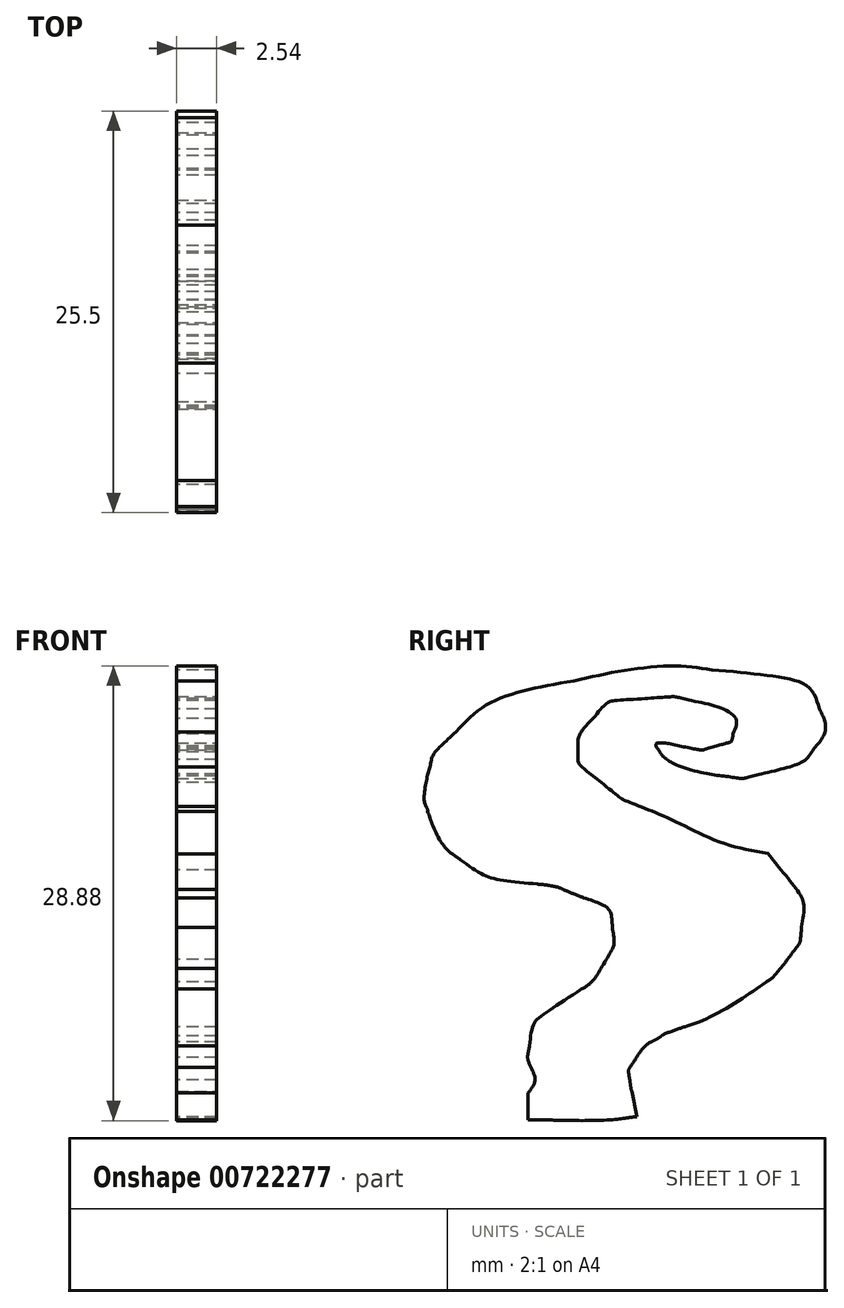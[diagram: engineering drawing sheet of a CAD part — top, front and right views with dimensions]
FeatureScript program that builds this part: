
annotation { "Feature Type Name" : "Feature", "Feature Type Description" : "" }
export const myFeature = defineFeature(function(context is Context, id is Id, definition is map)
    precondition{}
    {
        {
            var Q0;
            Q0=qCreatedBy(makeId("Right.planeOp"),FACE);
            var sketch = newSketch(context, id + "F0", { "sketchPlane" : qUnion([Q0])});
            skFitSpline(sketch, "E0", {"points": [v(-62.42, -40.65) * mm, v(-62.37, -40.57) * mm, v(-62.3, -40.5) * mm, v(-62.27, -40.5) * mm]});
            skFitSpline(sketch, "E1", {"points": [v(-62.27, -40.5) * mm, v(-62.23, -40.5) * mm, v(-62.2, -40.57) * mm, v(-62.2, -40.65) * mm]});
            skFitSpline(sketch, "E2", {"points": [v(-62.2, -40.65) * mm, v(-62.2, -40.73) * mm, v(-62.27, -40.8) * mm, v(-62.35, -40.8) * mm]});
            skFitSpline(sketch, "E3", {"points": [v(-62.35, -40.8) * mm, v(-62.44, -40.8) * mm, v(-62.46, -40.73) * mm, v(-62.42, -40.65) * mm]});
            skFitSpline(sketch, "E4", {"points": [v(6.95, -37.34) * mm, v(6.67, -37.22) * mm, v(6.74, -36.81) * mm, v(7.12, -36.25) * mm]});
            skFitSpline(sketch, "E5", {"points": [v(7.12, -36.25) * mm, v(7.31, -35.96) * mm, v(7.47, -35.66) * mm, v(7.47, -35.58) * mm]});
            skFitSpline(sketch, "E6", {"points": [v(7.47, -35.58) * mm, v(7.47, -35.5) * mm, v(7.56, -35.27) * mm, v(7.68, -35.06) * mm]});
            skFitSpline(sketch, "E7", {"points": [v(7.68, -35.06) * mm, v(7.79, -34.86) * mm, v(8.01, -34.38) * mm, v(8.17, -34) * mm]});
            skFitSpline(sketch, "E8", {"points": [v(8.17, -34) * mm, v(8.34, -33.6) * mm, v(8.53, -33.16) * mm, v(8.6, -33) * mm]});
            skFitSpline(sketch, "E9", {"points": [v(8.6, -33) * mm, v(8.67, -32.85) * mm, v(8.9, -32.16) * mm, v(9.13, -31.46) * mm]});
            skFitSpline(sketch, "E10", {"points": [v(9.13, -31.46) * mm, v(9.36, -30.76) * mm, v(9.6, -30.07) * mm, v(9.68, -29.92) * mm]});
            skFitSpline(sketch, "E11", {"points": [v(9.68, -29.92) * mm, v(9.76, -29.77) * mm, v(9.9, -29.36) * mm, v(9.99, -29.01) * mm]});
            skFitSpline(sketch, "E12", {"points": [v(9.99, -29.01) * mm, v(10.24, -28.04) * mm, v(10.5, -27.21) * mm, v(10.9, -26.14) * mm]});
            skFitSpline(sketch, "E13", {"points": [v(10.9, -26.14) * mm, v(11.1, -25.6) * mm, v(11.25, -25.03) * mm, v(11.25, -24.88) * mm]});
            skFitSpline(sketch, "E14", {"points": [v(11.25, -24.88) * mm, v(11.26, -24.72) * mm, v(11.38, -24.4) * mm, v(11.54, -24.18) * mm]});
            skFitSpline(sketch, "E15", {"points": [v(11.54, -24.18) * mm, v(11.7, -23.95) * mm, v(11.82, -23.56) * mm, v(11.82, -23.33) * mm]});
            skFitSpline(sketch, "E16", {"points": [v(11.82, -23.33) * mm, v(11.82, -23.1) * mm, v(11.91, -22.78) * mm, v(12.02, -22.63) * mm]});
            skFitSpline(sketch, "E17", {"points": [v(12.02, -22.63) * mm, v(12.14, -22.48) * mm, v(12.23, -22.2) * mm, v(12.23, -22) * mm]});
            skFitSpline(sketch, "E18", {"points": [v(12.23, -22) * mm, v(12.24, -21.8) * mm, v(12.33, -21.51) * mm, v(12.44, -21.36) * mm]});
            skFitSpline(sketch, "E19", {"points": [v(12.44, -21.36) * mm, v(12.56, -21.22) * mm, v(12.65, -20.87) * mm, v(12.65, -20.6) * mm]});
            skFitSpline(sketch, "E20", {"points": [v(12.65, -20.6) * mm, v(12.66, -20.33) * mm, v(12.74, -19.98) * mm, v(12.85, -19.83) * mm]});
            skFitSpline(sketch, "E21", {"points": [v(12.85, -19.83) * mm, v(12.95, -19.67) * mm, v(13.08, -19.3) * mm, v(13.12, -19) * mm]});
            skFitSpline(sketch, "E22", {"points": [v(13.12, -19) * mm, v(13.17, -18.7) * mm, v(13.33, -18.14) * mm, v(13.48, -17.74) * mm]});
            skFitSpline(sketch, "E23", {"points": [v(13.48, -17.74) * mm, v(13.92, -16.59) * mm, v(14.06, -16.05) * mm, v(14.06, -15.6) * mm]});
            skFitSpline(sketch, "E24", {"points": [v(14.06, -15.6) * mm, v(14.06, -15.36) * mm, v(14.19, -15.01) * mm, v(14.34, -14.81) * mm]});
            skFitSpline(sketch, "E25", {"points": [v(14.34, -14.81) * mm, v(14.51, -14.6) * mm, v(14.61, -14.28) * mm, v(14.6, -14.03) * mm]});
            skFitSpline(sketch, "E26", {"points": [v(14.6, -14.03) * mm, v(14.58, -13.78) * mm, v(14.67, -13.5) * mm, v(14.83, -13.32) * mm]});
            skFitSpline(sketch, "E27", {"points": [v(14.83, -13.32) * mm, v(14.98, -13.14) * mm, v(15.04, -12.98) * mm, v(14.96, -12.9) * mm]});
            skFitSpline(sketch, "E28", {"points": [v(14.96, -12.9) * mm, v(14.9, -12.85) * mm, v(14.01, -12.72) * mm, v(13, -12.63) * mm]});
            skFitSpline(sketch, "E29", {"points": [v(13, -12.63) * mm, v(10.97, -12.45) * mm, v(10.77, -12.35) * mm, v(10.99, -11.58) * mm]});
            skFitSpline(sketch, "E30", {"points": [v(10.99, -11.58) * mm, v(11.06, -11.34) * mm, v(11.23, -10.98) * mm, v(11.38, -10.79) * mm]});
            skFitSpline(sketch, "E31", {"points": [v(11.38, -10.79) * mm, v(11.63, -10.45) * mm, v(11.7, -10.44) * mm, v(13.33, -10.41) * mm]});
            skFitSpline(sketch, "E32", {"points": [v(13.33, -10.41) * mm, v(15.37, -10.38) * mm, v(15.88, -10.2) * mm, v(15.88, -9.49) * mm]});
            skFitSpline(sketch, "E33", {"points": [v(15.88, -9.49) * mm, v(15.88, -9.24) * mm, v(16.01, -8.85) * mm, v(16.16, -8.62) * mm]});
            skFitSpline(sketch, "E34", {"points": [v(16.16, -8.62) * mm, v(16.32, -8.38) * mm, v(16.44, -8.06) * mm, v(16.44, -7.9) * mm]});
            skFitSpline(sketch, "E35", {"points": [v(16.44, -7.9) * mm, v(16.44, -7.73) * mm, v(16.53, -7.52) * mm, v(16.65, -7.43) * mm]});
            skFitSpline(sketch, "E36", {"points": [v(16.65, -7.43) * mm, v(16.76, -7.34) * mm, v(16.89, -7.08) * mm, v(16.93, -6.86) * mm]});
            skFitSpline(sketch, "E37", {"points": [v(16.93, -6.86) * mm, v(16.98, -6.64) * mm, v(17.11, -6.39) * mm, v(17.22, -6.3) * mm]});
            skFitSpline(sketch, "E38", {"points": [v(17.22, -6.3) * mm, v(17.33, -6.2) * mm, v(17.43, -6.07) * mm, v(17.43, -6) * mm]});
            skFitSpline(sketch, "E39", {"points": [v(17.43, -6) * mm, v(17.43, -5.66) * mm, v(19.5, -3.04) * mm, v(20.14, -2.56) * mm]});
            skFitSpline(sketch, "E40", {"points": [v(20.14, -2.56) * mm, v(21.45, -1.6) * mm, v(22.48, -0.98) * mm, v(23.02, -0.84) * mm]});
            skFitSpline(sketch, "E41", {"points": [v(23.02, -0.84) * mm, v(23.36, -0.75) * mm, v(23.77, -0.59) * mm, v(23.93, -0.49) * mm]});
            skFitSpline(sketch, "E42", {"points": [v(23.93, -0.49) * mm, v(24.1, -0.38) * mm, v(24.92, -0.26) * mm, v(25.86, -0.2) * mm]});
            skFitSpline(sketch, "E43", {"points": [v(25.86, -0.2) * mm, v(27.2, -0.13) * mm, v(27.57, -0.15) * mm, v(27.92, -0.33) * mm]});
            skFitSpline(sketch, "E44", {"points": [v(27.92, -0.33) * mm, v(28.16, -0.46) * mm, v(28.58, -0.55) * mm, v(28.86, -0.55) * mm]});
            skFitSpline(sketch, "E45", {"points": [v(28.86, -0.55) * mm, v(29.16, -0.55) * mm, v(29.52, -0.67) * mm, v(29.72, -0.83) * mm]});
            skFitSpline(sketch, "E46", {"points": [v(29.72, -0.83) * mm, v(29.92, -0.99) * mm, v(30.16, -1.11) * mm, v(30.27, -1.11) * mm]});
            skFitSpline(sketch, "E47", {"points": [v(30.27, -1.11) * mm, v(30.5, -1.11) * mm, v(31.44, -1.93) * mm, v(31.44, -2.14) * mm]});
            skFitSpline(sketch, "E48", {"points": [v(31.44, -2.14) * mm, v(31.44, -2.22) * mm, v(31.56, -2.42) * mm, v(31.7, -2.58) * mm]});
            skFitSpline(sketch, "E49", {"points": [v(31.7, -2.58) * mm, v(31.89, -2.78) * mm, v(32, -3.16) * mm, v(32.04, -3.81) * mm]});
            skFitSpline(sketch, "E50", {"points": [v(32.04, -3.81) * mm, v(32.1, -4.6) * mm, v(32.07, -4.8) * mm, v(31.85, -5.06) * mm]});
            skFitSpline(sketch, "E51", {"points": [v(31.85, -5.06) * mm, v(31.7, -5.23) * mm, v(31.58, -5.46) * mm, v(31.58, -5.59) * mm]});
            skFitSpline(sketch, "E52", {"points": [v(31.58, -5.59) * mm, v(31.57, -5.94) * mm, v(30.98, -6.52) * mm, v(30.24, -6.92) * mm]});
            skFitSpline(sketch, "E53", {"points": [v(30.24, -6.92) * mm, v(29.43, -7.35) * mm, v(29.36, -7.35) * mm, v(28.2, -7.06) * mm]});
            skFitSpline(sketch, "E54", {"points": [v(28.2, -7.06) * mm, v(27.03, -6.76) * mm, v(26.89, -6.67) * mm, v(26.4, -6) * mm]});
            skFitSpline(sketch, "E55", {"points": [v(26.4, -6) * mm, v(25.84, -5.23) * mm, v(25.86, -4.7) * mm, v(26.48, -3.42) * mm]});
            skFitSpline(sketch, "E56", {"points": [v(26.48, -3.42) * mm, v(26.76, -2.85) * mm, v(26.95, -2.29) * mm, v(26.9, -2.17) * mm]});
            skFitSpline(sketch, "E57", {"points": [v(26.9, -2.17) * mm, v(26.78, -1.82) * mm, v(25.62, -1.89) * mm, v(25.1, -2.27) * mm]});
            skFitSpline(sketch, "E58", {"points": [v(25.1, -2.27) * mm, v(23.94, -3.14) * mm, v(22.61, -5.14) * mm, v(22.61, -6.04) * mm]});
            skFitSpline(sketch, "E59", {"points": [v(22.61, -6.04) * mm, v(22.61, -6.24) * mm, v(22.52, -6.49) * mm, v(22.4, -6.58) * mm]});
            skFitSpline(sketch, "E60", {"points": [v(22.4, -6.58) * mm, v(22.3, -6.67) * mm, v(22.16, -6.98) * mm, v(22.12, -7.26) * mm]});
            skFitSpline(sketch, "E61", {"points": [v(22.12, -7.26) * mm, v(22.07, -7.54) * mm, v(21.94, -8) * mm, v(21.84, -8.26) * mm]});
            skFitSpline(sketch, "E62", {"points": [v(21.84, -8.26) * mm, v(21.67, -8.68) * mm, v(21.57, -9.63) * mm, v(21.62, -10.34) * mm]});
            skFitSpline(sketch, "E63", {"points": [v(21.62, -10.34) * mm, v(21.63, -10.5) * mm, v(22.02, -10.52) * mm, v(23.65, -10.45) * mm]});
            skFitSpline(sketch, "E64", {"points": [v(23.65, -10.45) * mm, v(24.75, -10.4) * mm, v(25.76, -10.34) * mm, v(25.88, -10.29) * mm]});
            skFitSpline(sketch, "E65", {"points": [v(25.88, -10.29) * mm, v(26.45, -10.07) * mm, v(26.93, -10.83) * mm, v(26.47, -11.2) * mm]});
            skFitSpline(sketch, "E66", {"points": [v(26.47, -11.2) * mm, v(26.35, -11.3) * mm, v(26.26, -11.6) * mm, v(26.26, -11.85) * mm]});
            skFitSpline(sketch, "E67", {"points": [v(26.26, -11.85) * mm, v(26.26, -12.6) * mm, v(25.78, -12.72) * mm, v(22.8, -12.8) * mm]});
            skFitSpline(sketch, "E68", {"points": [v(22.8, -12.8) * mm, v(21.06, -12.85) * mm, v(20.79, -12.96) * mm, v(20.79, -13.62) * mm]});
            skFitSpline(sketch, "E69", {"points": [v(20.79, -13.62) * mm, v(20.79, -13.85) * mm, v(20.71, -14.17) * mm, v(20.62, -14.34) * mm]});
            skFitSpline(sketch, "E70", {"points": [v(20.62, -14.34) * mm, v(20.53, -14.5) * mm, v(20.41, -14.93) * mm, v(20.36, -15.27) * mm]});
            skFitSpline(sketch, "E71", {"points": [v(20.36, -15.27) * mm, v(20.3, -15.62) * mm, v(20.2, -16.1) * mm, v(20.12, -16.33) * mm]});
            skFitSpline(sketch, "E72", {"points": [v(20.12, -16.33) * mm, v(20.04, -16.56) * mm, v(19.9, -17.01) * mm, v(19.82, -17.34) * mm]});
            skFitSpline(sketch, "E73", {"points": [v(19.82, -17.34) * mm, v(19.74, -17.67) * mm, v(19.6, -18.2) * mm, v(19.51, -18.53) * mm]});
            skFitSpline(sketch, "E74", {"points": [v(19.51, -18.53) * mm, v(19.43, -18.86) * mm, v(19.27, -19.3) * mm, v(19.16, -19.53) * mm]});
            skFitSpline(sketch, "E75", {"points": [v(19.16, -19.53) * mm, v(19.06, -19.75) * mm, v(18.97, -20.14) * mm, v(18.97, -20.41) * mm]});
            skFitSpline(sketch, "E76", {"points": [v(18.97, -20.41) * mm, v(18.97, -20.68) * mm, v(18.9, -21.02) * mm, v(18.82, -21.17) * mm]});
            skFitSpline(sketch, "E77", {"points": [v(18.82, -21.17) * mm, v(18.74, -21.33) * mm, v(18.54, -21.94) * mm, v(18.39, -22.53) * mm]});
            skFitSpline(sketch, "E78", {"points": [v(18.39, -22.53) * mm, v(17.96, -24.13) * mm, v(17.9, -24.36) * mm, v(17.57, -25.44) * mm]});
            skFitSpline(sketch, "E79", {"points": [v(17.57, -25.44) * mm, v(17.4, -25.98) * mm, v(17.2, -26.7) * mm, v(17.14, -27.05) * mm]});
            skFitSpline(sketch, "E80", {"points": [v(17.14, -27.05) * mm, v(17.06, -27.4) * mm, v(16.91, -27.87) * mm, v(16.8, -28.1) * mm]});
            skFitSpline(sketch, "E81", {"points": [v(16.8, -28.1) * mm, v(16.7, -28.33) * mm, v(16.5, -29) * mm, v(16.37, -29.57) * mm]});
            skFitSpline(sketch, "E82", {"points": [v(16.37, -29.57) * mm, v(16.23, -30.15) * mm, v(16.03, -30.75) * mm, v(15.93, -30.9) * mm]});
            skFitSpline(sketch, "E83", {"points": [v(15.93, -30.9) * mm, v(15.83, -31.05) * mm, v(15.74, -31.37) * mm, v(15.74, -31.6) * mm]});
            skFitSpline(sketch, "E84", {"points": [v(15.74, -31.6) * mm, v(15.74, -31.84) * mm, v(15.65, -32.2) * mm, v(15.54, -32.42) * mm]});
            skFitSpline(sketch, "E85", {"points": [v(15.54, -32.42) * mm, v(15.42, -32.63) * mm, v(15.3, -33.04) * mm, v(15.24, -33.33) * mm]});
            skFitSpline(sketch, "E86", {"points": [v(15.24, -33.33) * mm, v(15.19, -33.62) * mm, v(15.08, -33.93) * mm, v(15, -34.03) * mm]});
            skFitSpline(sketch, "E87", {"points": [v(15, -34.03) * mm, v(14.93, -34.12) * mm, v(14.81, -34.5) * mm, v(14.74, -34.85) * mm]});
            skFitSpline(sketch, "E88", {"points": [v(14.74, -34.85) * mm, v(14.68, -35.21) * mm, v(14.46, -35.72) * mm, v(14.26, -35.97) * mm]});
            skFitSpline(sketch, "E89", {"points": [v(14.26, -35.97) * mm, v(13.94, -36.4) * mm, v(13.83, -36.45) * mm, v(13.18, -36.45) * mm]});
            skFitSpline(sketch, "E90", {"points": [v(13.18, -36.45) * mm, v(12.25, -36.47) * mm, v(11.28, -36.63) * mm, v(10.14, -36.97) * mm]});
            skFitSpline(sketch, "E91", {"points": [v(10.14, -36.97) * mm, v(9.2, -37.25) * mm, v(7.26, -37.47) * mm, v(6.95, -37.34) * mm]});
            skFitSpline(sketch, "E92", {"points": [v(17.14, -9.54) * mm, v(17.14, -9.39) * mm, v(17.22, -9.18) * mm, v(17.32, -9.08) * mm]});
            skFitSpline(sketch, "E93", {"points": [v(17.32, -9.08) * mm, v(17.6, -8.8) * mm, v(18.97, -6.5) * mm, v(18.97, -6.33) * mm]});
            skFitSpline(sketch, "E94", {"points": [v(18.97, -6.33) * mm, v(18.97, -6.25) * mm, v(19.09, -6.1) * mm, v(19.23, -6) * mm]});
            skFitSpline(sketch, "E95", {"points": [v(19.23, -6) * mm, v(19.37, -5.9) * mm, v(19.62, -5.58) * mm, v(19.77, -5.3) * mm]});
            skFitSpline(sketch, "E96", {"points": [v(19.77, -5.3) * mm, v(19.92, -5) * mm, v(20.23, -4.59) * mm, v(20.45, -4.37) * mm]});
            skFitSpline(sketch, "E97", {"points": [v(20.45, -4.37) * mm, v(21.4, -3.43) * mm, v(22.2, -2.53) * mm, v(22.2, -2.39) * mm]});
            skFitSpline(sketch, "E98", {"points": [v(22.2, -2.39) * mm, v(22.2, -2.3) * mm, v(22.04, -2.24) * mm, v(21.86, -2.24) * mm]});
            skFitSpline(sketch, "E99", {"points": [v(21.86, -2.24) * mm, v(21.62, -2.24) * mm, v(21.16, -2.62) * mm, v(20.24, -3.58) * mm]});
            skFitSpline(sketch, "E100", {"points": [v(20.24, -3.58) * mm, v(18.6, -5.29) * mm, v(18.2, -5.92) * mm, v(17.21, -8.2) * mm]});
            skFitSpline(sketch, "E101", {"points": [v(17.21, -8.2) * mm, v(16.68, -9.43) * mm, v(16.61, -9.8) * mm, v(16.93, -9.8) * mm]});
            skFitSpline(sketch, "E102", {"points": [v(16.93, -9.8) * mm, v(17.05, -9.8) * mm, v(17.14, -9.69) * mm, v(17.14, -9.54) * mm]});
            skFitSpline(sketch, "E103", {"points": [v(29, -29.64) * mm, v(28.68, -29.53) * mm, v(28.25, -29.44) * mm, v(28.04, -29.44) * mm]});
            skFitSpline(sketch, "E104", {"points": [v(28.04, -29.44) * mm, v(27.82, -29.44) * mm, v(27.4, -29.3) * mm, v(27.1, -29.15) * mm]});
            skFitSpline(sketch, "E105", {"points": [v(27.1, -29.15) * mm, v(26.8, -29) * mm, v(26.48, -28.87) * mm, v(26.4, -28.87) * mm]});
            skFitSpline(sketch, "E106", {"points": [v(26.4, -28.87) * mm, v(26.13, -28.87) * mm, v(24.74, -27.9) * mm, v(24.42, -27.47) * mm]});
            skFitSpline(sketch, "E107", {"points": [v(24.42, -27.47) * mm, v(24.23, -27.23) * mm, v(23.92, -26.84) * mm, v(23.72, -26.6) * mm]});
            skFitSpline(sketch, "E108", {"points": [v(23.72, -26.6) * mm, v(23.52, -26.34) * mm, v(23.14, -25.74) * mm, v(22.89, -25.24) * mm]});
            skFitSpline(sketch, "E109", {"points": [v(22.89, -25.24) * mm, v(22.45, -24.4) * mm, v(22.42, -24.23) * mm, v(22.34, -22.51) * mm]});
            skFitSpline(sketch, "E110", {"points": [v(22.34, -22.51) * mm, v(22.26, -20.9) * mm, v(22.28, -20.6) * mm, v(22.5, -20.15) * mm]});
            skFitSpline(sketch, "E111", {"points": [v(22.5, -20.15) * mm, v(22.64, -19.87) * mm, v(22.75, -19.54) * mm, v(22.75, -19.43) * mm]});
            skFitSpline(sketch, "E112", {"points": [v(22.75, -19.43) * mm, v(22.75, -19.33) * mm, v(22.88, -19.08) * mm, v(23.03, -18.88) * mm]});
            skFitSpline(sketch, "E113", {"points": [v(23.03, -18.88) * mm, v(23.19, -18.69) * mm, v(23.31, -18.4) * mm, v(23.31, -18.23) * mm]});
            skFitSpline(sketch, "E114", {"points": [v(23.31, -18.23) * mm, v(23.31, -18.06) * mm, v(23.57, -17.61) * mm, v(23.87, -17.22) * mm]});
            skFitSpline(sketch, "E115", {"points": [v(23.87, -17.22) * mm, v(24.18, -16.83) * mm, v(24.44, -16.46) * mm, v(24.44, -16.4) * mm]});
            skFitSpline(sketch, "E116", {"points": [v(24.44, -16.4) * mm, v(24.44, -16.3) * mm, v(25.2, -15.67) * mm, v(26.88, -14.37) * mm]});
            skFitSpline(sketch, "E117", {"points": [v(26.88, -14.37) * mm, v(27.03, -14.25) * mm, v(27.26, -14.15) * mm, v(27.39, -14.15) * mm]});
            skFitSpline(sketch, "E118", {"points": [v(27.39, -14.15) * mm, v(27.51, -14.15) * mm, v(27.73, -14.03) * mm, v(27.86, -13.88) * mm]});
            skFitSpline(sketch, "E119", {"points": [v(27.86, -13.88) * mm, v(28, -13.73) * mm, v(28.37, -13.57) * mm, v(28.69, -13.52) * mm]});
            skFitSpline(sketch, "E120", {"points": [v(28.69, -13.52) * mm, v(29, -13.47) * mm, v(29.46, -13.3) * mm, v(29.7, -13.17) * mm]});
            skFitSpline(sketch, "E121", {"points": [v(29.7, -13.17) * mm, v(29.92, -13.03) * mm, v(30.52, -12.87) * mm, v(31.02, -12.81) * mm]});
            skFitSpline(sketch, "E122", {"points": [v(31.02, -12.81) * mm, v(31.53, -12.76) * mm, v(32.2, -12.6) * mm, v(32.5, -12.46) * mm]});
            skFitSpline(sketch, "E123", {"points": [v(32.5, -12.46) * mm, v(33.19, -12.16) * mm, v(35.4, -12.07) * mm, v(36.35, -12.3) * mm]});
            skFitSpline(sketch, "E124", {"points": [v(36.35, -12.3) * mm, v(36.7, -12.4) * mm, v(37.27, -12.47) * mm, v(37.61, -12.47) * mm]});
            skFitSpline(sketch, "E125", {"points": [v(37.61, -12.47) * mm, v(38.8, -12.47) * mm, v(40.72, -13.41) * mm, v(41.31, -14.27) * mm]});
            skFitSpline(sketch, "E126", {"points": [v(41.31, -14.27) * mm, v(41.6, -14.7) * mm, v(41.68, -14.96) * mm, v(41.68, -15.64) * mm]});
            skFitSpline(sketch, "E127", {"points": [v(41.68, -15.64) * mm, v(41.68, -16.36) * mm, v(41.6, -16.58) * mm, v(41.19, -17.24) * mm]});
            skFitSpline(sketch, "E128", {"points": [v(41.19, -17.24) * mm, v(40.92, -17.66) * mm, v(40.7, -18.05) * mm, v(40.7, -18.12) * mm]});
            skFitSpline(sketch, "E129", {"points": [v(40.7, -18.12) * mm, v(40.7, -18.18) * mm, v(40.47, -18.33) * mm, v(40.2, -18.44) * mm]});
            skFitSpline(sketch, "E130", {"points": [v(40.2, -18.44) * mm, v(39.93, -18.55) * mm, v(39.67, -18.74) * mm, v(39.63, -18.84) * mm]});
            skFitSpline(sketch, "E131", {"points": [v(39.63, -18.84) * mm, v(39.54, -19.07) * mm, v(37.94, -20.05) * mm, v(37, -20.45) * mm]});
            skFitSpline(sketch, "E132", {"points": [v(37, -20.45) * mm, v(36.66, -20.6) * mm, v(36.34, -20.79) * mm, v(36.29, -20.87) * mm]});
            skFitSpline(sketch, "E133", {"points": [v(36.29, -20.87) * mm, v(36.24, -20.95) * mm, v(36.06, -21.02) * mm, v(35.89, -21.02) * mm]});
            skFitSpline(sketch, "E134", {"points": [v(35.89, -21.02) * mm, v(35.72, -21.02) * mm, v(35.38, -21.15) * mm, v(35.12, -21.3) * mm]});
            skFitSpline(sketch, "E135", {"points": [v(35.12, -21.3) * mm, v(34.87, -21.45) * mm, v(34.37, -21.65) * mm, v(34, -21.74) * mm]});
            skFitSpline(sketch, "E136", {"points": [v(34, -21.74) * mm, v(33.64, -21.83) * mm, v(33.1, -22.02) * mm, v(32.82, -22.16) * mm]});
            skFitSpline(sketch, "E137", {"points": [v(32.82, -22.16) * mm, v(32.53, -22.3) * mm, v(32.09, -22.42) * mm, v(31.84, -22.43) * mm]});
            skFitSpline(sketch, "E138", {"points": [v(31.84, -22.43) * mm, v(31.26, -22.43) * mm, v(29.76, -23.03) * mm, v(29.52, -23.35) * mm]});
            skFitSpline(sketch, "E139", {"points": [v(29.52, -23.35) * mm, v(29.28, -23.68) * mm, v(29.3, -24.53) * mm, v(29.54, -24.89) * mm]});
            skFitSpline(sketch, "E140", {"points": [v(29.54, -24.89) * mm, v(29.65, -25.04) * mm, v(29.8, -25.44) * mm, v(29.9, -25.76) * mm]});
            skFitSpline(sketch, "E141", {"points": [v(29.9, -25.76) * mm, v(30.08, -26.43) * mm, v(30.68, -26.9) * mm, v(31.33, -26.91) * mm]});
            skFitSpline(sketch, "E142", {"points": [v(31.33, -26.91) * mm, v(31.54, -26.91) * mm, v(31.75, -26.97) * mm, v(31.8, -27.05) * mm]});
            skFitSpline(sketch, "E143", {"points": [v(31.8, -27.05) * mm, v(31.92, -27.26) * mm, v(32.9, -27.22) * mm, v(33.5, -26.99) * mm]});
            skFitSpline(sketch, "E144", {"points": [v(33.5, -26.99) * mm, v(33.8, -26.88) * mm, v(34.32, -26.71) * mm, v(34.67, -26.62) * mm]});
            skFitSpline(sketch, "E145", {"points": [v(34.67, -26.62) * mm, v(35.01, -26.54) * mm, v(35.47, -26.31) * mm, v(35.7, -26.13) * mm]});
            skFitSpline(sketch, "E146", {"points": [v(35.7, -26.13) * mm, v(35.91, -25.94) * mm, v(36.14, -25.79) * mm, v(36.2, -25.79) * mm]});
            skFitSpline(sketch, "E147", {"points": [v(36.2, -25.79) * mm, v(36.42, -25.79) * mm, v(38.35, -23.75) * mm, v(38.6, -23.24) * mm]});
            skFitSpline(sketch, "E148", {"points": [v(38.6, -23.24) * mm, v(38.76, -22.94) * mm, v(38.91, -22.7) * mm, v(38.95, -22.7) * mm]});
            skFitSpline(sketch, "E149", {"points": [v(38.95, -22.7) * mm, v(39, -22.7) * mm, v(39.28, -22.83) * mm, v(39.58, -22.99) * mm]});
            skFitSpline(sketch, "E150", {"points": [v(39.58, -22.99) * mm, v(40.22, -23.31) * mm, v(40.28, -23.57) * mm, v(39.8, -24) * mm]});
            skFitSpline(sketch, "E151", {"points": [v(39.8, -24) * mm, v(39.62, -24.18) * mm, v(39.35, -24.56) * mm, v(39.2, -24.85) * mm]});
            skFitSpline(sketch, "E152", {"points": [v(39.2, -24.85) * mm, v(38.87, -25.5) * mm, v(37.62, -27) * mm, v(37.33, -27.11) * mm]});
            skFitSpline(sketch, "E153", {"points": [v(37.33, -27.11) * mm, v(37.2, -27.16) * mm, v(36.83, -27.44) * mm, v(36.5, -27.75) * mm]});
            skFitSpline(sketch, "E154", {"points": [v(36.5, -27.75) * mm, v(36.15, -28.06) * mm, v(35.82, -28.31) * mm, v(35.75, -28.31) * mm]});
            skFitSpline(sketch, "E155", {"points": [v(35.75, -28.31) * mm, v(35.68, -28.31) * mm, v(35.43, -28.47) * mm, v(35.2, -28.66) * mm]});
            skFitSpline(sketch, "E156", {"points": [v(35.2, -28.66) * mm, v(34.98, -28.86) * mm, v(34.61, -29.01) * mm, v(34.4, -29.01) * mm]});
            skFitSpline(sketch, "E157", {"points": [v(34.4, -29.01) * mm, v(34.18, -29.01) * mm, v(33.85, -29.14) * mm, v(33.66, -29.29) * mm]});
            skFitSpline(sketch, "E158", {"points": [v(33.66, -29.29) * mm, v(33.4, -29.5) * mm, v(32.93, -29.6) * mm, v(31.64, -29.7) * mm]});
            skFitSpline(sketch, "E159", {"points": [v(31.64, -29.7) * mm, v(29.6, -29.89) * mm, v(29.68, -29.89) * mm, v(29, -29.64) * mm]});
            skFitSpline(sketch, "E160", {"points": [v(30.67, -21.02) * mm, v(30.81, -20.87) * mm, v(31.06, -20.74) * mm, v(31.22, -20.74) * mm]});
            skFitSpline(sketch, "E161", {"points": [v(31.22, -20.74) * mm, v(31.64, -20.74) * mm, v(33.87, -19.15) * mm, v(34.44, -18.46) * mm]});
            skFitSpline(sketch, "E162", {"points": [v(34.44, -18.46) * mm, v(34.7, -18.13) * mm, v(35.18, -17.34) * mm, v(35.51, -16.7) * mm]});
            skFitSpline(sketch, "E163", {"points": [v(35.51, -16.7) * mm, v(36.01, -15.72) * mm, v(36.1, -15.45) * mm, v(36.03, -14.96) * mm]});
            skFitSpline(sketch, "E164", {"points": [v(36.03, -14.96) * mm, v(35.92, -14.12) * mm, v(35.53, -13.8) * mm, v(34.63, -13.8) * mm]});
            skFitSpline(sketch, "E165", {"points": [v(34.63, -13.8) * mm, v(33.74, -13.81) * mm, v(33.12, -14.17) * mm, v(32.01, -15.3) * mm]});
            skFitSpline(sketch, "E166", {"points": [v(32.01, -15.3) * mm, v(31.15, -16.2) * mm, v(30.65, -16.92) * mm, v(30.52, -17.5) * mm]});
            skFitSpline(sketch, "E167", {"points": [v(30.52, -17.5) * mm, v(30.47, -17.7) * mm, v(30.33, -17.98) * mm, v(30.22, -18.1) * mm]});
            skFitSpline(sketch, "E168", {"points": [v(30.22, -18.1) * mm, v(30.09, -18.26) * mm, v(30.03, -18.52) * mm, v(30.08, -18.8) * mm]});
            skFitSpline(sketch, "E169", {"points": [v(30.08, -18.8) * mm, v(30.11, -19.06) * mm, v(30.05, -19.63) * mm, v(29.94, -20.08) * mm]});
            skFitSpline(sketch, "E170", {"points": [v(29.94, -20.08) * mm, v(29.83, -20.53) * mm, v(29.77, -20.98) * mm, v(29.81, -21.1) * mm]});
            skFitSpline(sketch, "E171", {"points": [v(29.81, -21.1) * mm, v(29.93, -21.4) * mm, v(30.38, -21.35) * mm, v(30.67, -21.02) * mm]});
            skFitSpline(sketch, "E172", {"points": [v(24.44, -19.34) * mm, v(24.44, -19.1) * mm, v(24.5, -18.92) * mm, v(24.57, -18.92) * mm]});
            skFitSpline(sketch, "E173", {"points": [v(24.57, -18.92) * mm, v(24.64, -18.92) * mm, v(25.14, -18.4) * mm, v(25.68, -17.76) * mm]});
            skFitSpline(sketch, "E174", {"points": [v(25.68, -17.76) * mm, v(26.9, -16.33) * mm, v(27.23, -16) * mm, v(28.3, -15.19) * mm]});
            skFitSpline(sketch, "E175", {"points": [v(28.3, -15.19) * mm, v(28.75, -14.83) * mm, v(29.13, -14.47) * mm, v(29.13, -14.38) * mm]});
            skFitSpline(sketch, "E176", {"points": [v(29.13, -14.38) * mm, v(29.13, -14.12) * mm, v(28.22, -14.24) * mm, v(27.88, -14.56) * mm]});
            skFitSpline(sketch, "E177", {"points": [v(27.88, -14.56) * mm, v(27.71, -14.72) * mm, v(27.5, -14.85) * mm, v(27.4, -14.85) * mm]});
            skFitSpline(sketch, "E178", {"points": [v(27.4, -14.85) * mm, v(26.9, -14.85) * mm, v(24.44, -17.88) * mm, v(24.44, -18.5) * mm]});
            skFitSpline(sketch, "E179", {"points": [v(24.44, -18.5) * mm, v(24.44, -18.64) * mm, v(24.34, -18.82) * mm, v(24.22, -18.92) * mm]});
            skFitSpline(sketch, "E180", {"points": [v(24.22, -18.92) * mm, v(24.1, -19.02) * mm, v(24.01, -19.24) * mm, v(24.01, -19.43) * mm]});
            skFitSpline(sketch, "E181", {"points": [v(24.01, -19.43) * mm, v(24.01, -19.63) * mm, v(24.1, -19.76) * mm, v(24.22, -19.76) * mm]});
            skFitSpline(sketch, "E182", {"points": [v(24.22, -19.76) * mm, v(24.36, -19.76) * mm, v(24.44, -19.62) * mm, v(24.44, -19.34) * mm]});
            skFitSpline(sketch, "E183", {"points": [v(-26.74, -28.83) * mm, v(-27.67, -28.42) * mm, v(-28.08, -28.18) * mm, v(-29.33, -27.33) * mm]});
            skFitSpline(sketch, "E184", {"points": [v(-29.33, -27.33) * mm, v(-29.7, -27.08) * mm, v(-30.66, -26.07) * mm, v(-30.66, -25.93) * mm]});
            skFitSpline(sketch, "E185", {"points": [v(-30.66, -25.93) * mm, v(-30.66, -25.88) * mm, v(-30.85, -25.57) * mm, v(-31.08, -25.25) * mm]});
            skFitSpline(sketch, "E186", {"points": [v(-31.08, -25.25) * mm, v(-31.31, -24.93) * mm, v(-31.5, -24.6) * mm, v(-31.5, -24.52) * mm]});
            skFitSpline(sketch, "E187", {"points": [v(-31.5, -24.52) * mm, v(-31.5, -24.44) * mm, v(-31.67, -24.05) * mm, v(-31.87, -23.66) * mm]});
            skFitSpline(sketch, "E188", {"points": [v(-32.15, -20.26) * mm, v(-32.07, -17.36) * mm, v(-31.96, -16.46) * mm, v(-31.53, -15.25) * mm]});
            skFitSpline(sketch, "E189", {"points": [v(-31.53, -15.25) * mm, v(-30.7, -12.9) * mm, v(-28.5, -9.7) * mm, v(-27.02, -8.69) * mm]});
            skFitSpline(sketch, "E190", {"points": [v(-27.02, -8.69) * mm, v(-26.75, -8.5) * mm, v(-26.44, -8.23) * mm, v(-26.34, -8.09) * mm]});
            skFitSpline(sketch, "E191", {"points": [v(-26.34, -8.09) * mm, v(-26.23, -7.94) * mm, v(-26.01, -7.77) * mm, v(-25.85, -7.7) * mm]});
            skFitSpline(sketch, "E192", {"points": [v(-25.85, -7.7) * mm, v(-25.68, -7.62) * mm, v(-25.2, -7.3) * mm, v(-24.77, -7) * mm]});
            skFitSpline(sketch, "E193", {"points": [v(-24.77, -7) * mm, v(-24.35, -6.7) * mm, v(-23.94, -6.44) * mm, v(-23.86, -6.44) * mm]});
            skFitSpline(sketch, "E194", {"points": [v(-23.86, -6.44) * mm, v(-23.79, -6.44) * mm, v(-23.56, -6.31) * mm, v(-23.37, -6.16) * mm]});
            skFitSpline(sketch, "E195", {"points": [v(-23.37, -6.16) * mm, v(-23.18, -6.01) * mm, v(-22.8, -5.88) * mm, v(-22.53, -5.88) * mm]});
            skFitSpline(sketch, "E196", {"points": [v(-22.53, -5.88) * mm, v(-22.26, -5.88) * mm, v(-21.78, -5.76) * mm, v(-21.46, -5.61) * mm]});
            skFitSpline(sketch, "E197", {"points": [v(-21.46, -5.61) * mm, v(-21.15, -5.47) * mm, v(-20.61, -5.3) * mm, v(-20.27, -5.25) * mm]});
            skFitSpline(sketch, "E198", {"points": [v(-20.27, -5.25) * mm, v(-19.93, -5.2) * mm, v(-19.37, -5.01) * mm, v(-19.03, -4.84) * mm]});
            skFitSpline(sketch, "E199", {"points": [v(-19.03, -4.84) * mm, v(-17.92, -4.28) * mm, v(-14.35, -4.13) * mm, v(-14.04, -4.64) * mm]});
            skFitSpline(sketch, "E200", {"points": [v(-14.04, -4.64) * mm, v(-14, -4.7) * mm, v(-13.75, -4.76) * mm, v(-13.5, -4.76) * mm]});
            skFitSpline(sketch, "E201", {"points": [v(-13.5, -4.76) * mm, v(-13.22, -4.76) * mm, v(-12.94, -4.87) * mm, v(-12.79, -5.04) * mm]});
            skFitSpline(sketch, "E202", {"points": [v(-12.79, -5.04) * mm, v(-12.65, -5.2) * mm, v(-12.44, -5.32) * mm, v(-12.33, -5.32) * mm]});
            skFitSpline(sketch, "E203", {"points": [v(-12.33, -5.32) * mm, v(-11.66, -5.32) * mm, v(-9.3, -7.47) * mm, v(-9.18, -8.2) * mm]});
            skFitSpline(sketch, "E204", {"points": [v(-9.18, -8.2) * mm, v(-9.14, -8.43) * mm, v(-9, -8.91) * mm, v(-8.85, -9.28) * mm]});
            skFitSpline(sketch, "E205", {"points": [v(-8.85, -9.28) * mm, v(-8.6, -9.93) * mm, v(-8.6, -9.95) * mm, v(-8.9, -10.9) * mm]});
            skFitSpline(sketch, "E206", {"points": [v(-8.9, -10.9) * mm, v(-9.21, -11.86) * mm, v(-9.47, -12.2) * mm, v(-10.44, -12.87) * mm]});
            skFitSpline(sketch, "E207", {"points": [v(-10.44, -12.87) * mm, v(-10.8, -13.11) * mm, v(-11.16, -13.2) * mm, v(-11.94, -13.25) * mm]});
            skFitSpline(sketch, "E208", {"points": [v(-11.94, -13.25) * mm, v(-12.84, -13.3) * mm, v(-13.05, -13.26) * mm, v(-13.58, -12.96) * mm]});
            skFitSpline(sketch, "E209", {"points": [v(-13.58, -12.96) * mm, v(-14.28, -12.58) * mm, v(-14.7, -12.06) * mm, v(-15.1, -11.12) * mm]});
            skFitSpline(sketch, "E210", {"points": [v(-15.1, -11.12) * mm, v(-15.44, -10.35) * mm, v(-15.45, -9.47) * mm, v(-15.15, -7.83) * mm]});
            skFitSpline(sketch, "E211", {"points": [v(-15.15, -7.83) * mm, v(-14.85, -6.16) * mm, v(-14.88, -6.12) * mm, v(-16.49, -6.25) * mm]});
            skFitSpline(sketch, "E212", {"points": [v(-16.49, -6.25) * mm, v(-17.38, -6.31) * mm, v(-17.84, -6.43) * mm, v(-18.27, -6.67) * mm]});
            skFitSpline(sketch, "E213", {"points": [v(-18.27, -6.67) * mm, v(-18.58, -6.85) * mm, v(-18.93, -7) * mm, v(-19.04, -7) * mm]});
            skFitSpline(sketch, "E214", {"points": [v(-19.04, -7) * mm, v(-19.27, -7) * mm, v(-20.79, -8.64) * mm, v(-21.22, -9.37) * mm]});
            skFitSpline(sketch, "E215", {"points": [v(-21.22, -9.37) * mm, v(-22.06, -10.76) * mm, v(-23.07, -13) * mm, v(-23.36, -14.08) * mm]});
            skFitSpline(sketch, "E216", {"points": [v(-23.36, -14.08) * mm, v(-23.42, -14.31) * mm, v(-23.58, -14.75) * mm, v(-23.7, -15.05) * mm]});
            skFitSpline(sketch, "E217", {"points": [v(-23.7, -15.05) * mm, v(-23.83, -15.34) * mm, v(-23.93, -15.7) * mm, v(-23.93, -15.83) * mm]});
            skFitSpline(sketch, "E218", {"points": [v(-23.93, -15.83) * mm, v(-23.93, -16.18) * mm, v(-24.47, -17.83) * mm, v(-24.64, -18) * mm]});
            skFitSpline(sketch, "E219", {"points": [v(-24.64, -18) * mm, v(-24.71, -18.07) * mm, v(-24.77, -18.33) * mm, v(-24.78, -18.56) * mm]});
            skFitSpline(sketch, "E220", {"points": [v(-24.78, -18.56) * mm, v(-24.78, -18.8) * mm, v(-24.9, -19.46) * mm, v(-25.06, -20.03) * mm]});
            skFitSpline(sketch, "E221", {"points": [v(-25.06, -20.03) * mm, v(-25.43, -21.44) * mm, v(-25.32, -23.66) * mm, v(-24.84, -24.23) * mm]});
            skFitSpline(sketch, "E222", {"points": [v(-24.84, -24.23) * mm, v(-24.67, -24.43) * mm, v(-24.49, -24.74) * mm, v(-24.43, -24.91) * mm]});
            skFitSpline(sketch, "E223", {"points": [v(-24.43, -24.91) * mm, v(-24.38, -25.09) * mm, v(-24.2, -25.3) * mm, v(-24.03, -25.39) * mm]});
            skFitSpline(sketch, "E224", {"points": [v(-24.03, -25.39) * mm, v(-23.86, -25.47) * mm, v(-23.6, -25.66) * mm, v(-23.44, -25.8) * mm]});
            skFitSpline(sketch, "E225", {"points": [v(-23.44, -25.8) * mm, v(-23, -26.18) * mm, v(-21.04, -26.35) * mm, v(-19.88, -26.1) * mm]});
            skFitSpline(sketch, "E226", {"points": [v(-19.88, -26.1) * mm, v(-18.77, -25.86) * mm, v(-17.45, -25.25) * mm, v(-16.27, -24.43) * mm]});
            skFitSpline(sketch, "E227", {"points": [v(-16.27, -24.43) * mm, v(-14.56, -23.23) * mm, v(-12.58, -20.97) * mm, v(-12.58, -20.21) * mm]});
            skFitSpline(sketch, "E228", {"points": [v(-12.58, -20.21) * mm, v(-12.58, -20.06) * mm, v(-12.5, -19.9) * mm, v(-12.4, -19.86) * mm]});
            skFitSpline(sketch, "E229", {"points": [v(-12.4, -19.86) * mm, v(-12.3, -19.82) * mm, v(-12.05, -19.44) * mm, v(-11.84, -19.02) * mm]});
            skFitSpline(sketch, "E230", {"points": [v(-11.84, -19.02) * mm, v(-11.63, -18.6) * mm, v(-11.3, -18.05) * mm, v(-11.09, -17.8) * mm]});
            skFitSpline(sketch, "E231", {"points": [v(-11.09, -17.8) * mm, v(-10.88, -17.56) * mm, v(-10.55, -17.11) * mm, v(-10.35, -16.82) * mm]});
            skFitSpline(sketch, "E232", {"points": [v(-10.35, -16.82) * mm, v(-9.94, -16.22) * mm, v(-7.64, -14.01) * mm, v(-7.41, -14.01) * mm]});
            skFitSpline(sketch, "E233", {"points": [v(-7.41, -14.01) * mm, v(-7.33, -14.01) * mm, v(-7.1, -13.87) * mm, v(-6.87, -13.69) * mm]});
            skFitSpline(sketch, "E234", {"points": [v(-6.87, -13.69) * mm, v(-6.23, -13.16) * mm, v(-5.05, -12.61) * mm, v(-4.56, -12.61) * mm]});
            skFitSpline(sketch, "E235", {"points": [v(-4.56, -12.61) * mm, v(-4.3, -12.61) * mm, v(-3.98, -12.5) * mm, v(-3.81, -12.33) * mm]});
            skFitSpline(sketch, "E236", {"points": [v(-3.81, -12.33) * mm, v(-3.55, -12.08) * mm, v(-3.25, -12.04) * mm, v(-1.54, -11.96) * mm]});
            skFitSpline(sketch, "E237", {"points": [v(-1.54, -11.96) * mm, v(0.15, -11.88) * mm, v(0.47, -11.9) * mm, v(0.75, -12.1) * mm]});
            skFitSpline(sketch, "E238", {"points": [v(0.75, -12.1) * mm, v(0.95, -12.24) * mm, v(1.37, -12.33) * mm, v(1.79, -12.33) * mm]});
            skFitSpline(sketch, "E239", {"points": [v(1.79, -12.33) * mm, v(2.18, -12.34) * mm, v(2.61, -12.43) * mm, v(2.75, -12.54) * mm]});
            skFitSpline(sketch, "E240", {"points": [v(2.75, -12.54) * mm, v(3.03, -12.75) * mm, v(3.33, -12.7) * mm, v(3.71, -12.36) * mm]});
            skFitSpline(sketch, "E241", {"points": [v(3.71, -12.36) * mm, v(3.87, -12.23) * mm, v(4.34, -12.15) * mm, v(5.05, -12.12) * mm]});
            skFitSpline(sketch, "E242", {"points": [v(5.05, -12.12) * mm, v(5.65, -12.1) * mm, v(6.78, -12.03) * mm, v(7.55, -11.98) * mm]});
            skFitSpline(sketch, "E243", {"points": [v(7.55, -11.98) * mm, v(9.42, -11.84) * mm, v(9.57, -11.9) * mm, v(9.57, -12.7) * mm]});
            skFitSpline(sketch, "E244", {"points": [v(9.57, -12.7) * mm, v(9.57, -13.04) * mm, v(9.45, -13.54) * mm, v(9.3, -13.84) * mm]});
            skFitSpline(sketch, "E245", {"points": [v(9.3, -13.84) * mm, v(9.14, -14.12) * mm, v(9.01, -14.49) * mm, v(9.01, -14.65) * mm]});
            skFitSpline(sketch, "E246", {"points": [v(9.01, -14.65) * mm, v(9.01, -14.8) * mm, v(8.92, -15.06) * mm, v(8.8, -15.21) * mm]});
            skFitSpline(sketch, "E247", {"points": [v(8.8, -15.21) * mm, v(8.7, -15.36) * mm, v(8.6, -15.67) * mm, v(8.6, -15.9) * mm]});
            skFitSpline(sketch, "E248", {"points": [v(8.6, -15.9) * mm, v(8.59, -16.14) * mm, v(8.5, -16.48) * mm, v(8.38, -16.68) * mm]});
            skFitSpline(sketch, "E249", {"points": [v(8.38, -16.68) * mm, v(8.27, -16.87) * mm, v(8.18, -17.17) * mm, v(8.18, -17.35) * mm]});
            skFitSpline(sketch, "E250", {"points": [v(8.18, -17.35) * mm, v(8.17, -17.52) * mm, v(8.05, -17.92) * mm, v(7.9, -18.22) * mm]});
            skFitSpline(sketch, "E251", {"points": [v(7.9, -18.22) * mm, v(7.74, -18.52) * mm, v(7.6, -18.91) * mm, v(7.6, -19.09) * mm]});
            skFitSpline(sketch, "E252", {"points": [v(7.6, -19.09) * mm, v(7.6, -19.27) * mm, v(7.51, -19.53) * mm, v(7.4, -19.68) * mm]});
            skFitSpline(sketch, "E253", {"points": [v(7.4, -19.68) * mm, v(7.28, -19.83) * mm, v(7.2, -20.08) * mm, v(7.2, -20.24) * mm]});
            skFitSpline(sketch, "E254", {"points": [v(7.2, -20.24) * mm, v(7.19, -20.4) * mm, v(7.1, -20.71) * mm, v(6.98, -20.93) * mm]});
            skFitSpline(sketch, "E255", {"points": [v(6.98, -20.93) * mm, v(6.86, -21.15) * mm, v(6.77, -21.52) * mm, v(6.77, -21.75) * mm]});
            skFitSpline(sketch, "E256", {"points": [v(6.77, -21.75) * mm, v(6.77, -21.98) * mm, v(6.64, -22.33) * mm, v(6.5, -22.53) * mm]});
            skFitSpline(sketch, "E257", {"points": [v(6.5, -22.53) * mm, v(6.34, -22.72) * mm, v(6.2, -23.09) * mm, v(6.2, -23.34) * mm]});
            skFitSpline(sketch, "E258", {"points": [v(6.2, -23.34) * mm, v(6.2, -23.59) * mm, v(6.12, -23.87) * mm, v(6, -23.97) * mm]});
            skFitSpline(sketch, "E259", {"points": [v(6, -23.97) * mm, v(5.86, -24.08) * mm, v(5.79, -24.4) * mm, v(5.79, -24.87) * mm]});
            skFitSpline(sketch, "E260", {"points": [v(5.79, -24.87) * mm, v(5.79, -25.7) * mm, v(6.04, -26.18) * mm, v(6.39, -25.98) * mm]});
            skFitSpline(sketch, "E261", {"points": [v(6.39, -25.98) * mm, v(6.83, -25.73) * mm, v(8.12, -24.4) * mm, v(8.73, -23.55) * mm]});
            skFitSpline(sketch, "E262", {"points": [v(8.73, -23.55) * mm, v(9.43, -22.57) * mm, v(9.77, -22.32) * mm, v(10.07, -22.57) * mm]});
            skFitSpline(sketch, "E263", {"points": [v(10.07, -22.57) * mm, v(10.5, -22.92) * mm, v(10.3, -23.42) * mm, v(9, -25.23) * mm]});
            skFitSpline(sketch, "E264", {"points": [v(9, -25.23) * mm, v(8.54, -25.85) * mm, v(7.1, -27.33) * mm, v(6.95, -27.33) * mm]});
            skFitSpline(sketch, "E265", {"points": [v(6.95, -27.33) * mm, v(6.9, -27.33) * mm, v(6.61, -27.54) * mm, v(6.3, -27.8) * mm]});
            skFitSpline(sketch, "E266", {"points": [v(6.3, -27.8) * mm, v(5.98, -28.05) * mm, v(5.26, -28.47) * mm, v(4.7, -28.73) * mm]});
            skFitSpline(sketch, "E267", {"points": [v(4.7, -28.73) * mm, v(3.8, -29.14) * mm, v(3.54, -29.2) * mm, v(2.39, -29.2) * mm]});
            skFitSpline(sketch, "E268", {"points": [v(2.39, -29.2) * mm, v(1.16, -29.22) * mm, v(1.06, -29.2) * mm, v(0.5, -28.8) * mm]});
            skFitSpline(sketch, "E269", {"points": [v(0.5, -28.8) * mm, v(0.12, -28.53) * mm, v(-0.14, -28.2) * mm, v(-0.24, -27.9) * mm]});
            skFitSpline(sketch, "E270", {"points": [v(-0.24, -27.9) * mm, v(-0.54, -26.95) * mm, v(-0.99, -26.07) * mm, v(-1.18, -26.07) * mm]});
            skFitSpline(sketch, "E271", {"points": [v(-1.18, -26.07) * mm, v(-1.28, -26.07) * mm, v(-1.5, -26.3) * mm, v(-1.66, -26.56) * mm]});
            skFitSpline(sketch, "E272", {"points": [v(-1.66, -26.56) * mm, v(-1.82, -26.83) * mm, v(-2, -27.05) * mm, v(-2.07, -27.05) * mm]});
            skFitSpline(sketch, "E273", {"points": [v(-2.07, -27.05) * mm, v(-2.13, -27.05) * mm, v(-2.6, -27.37) * mm, v(-3.12, -27.76) * mm]});
            skFitSpline(sketch, "E274", {"points": [v(-3.12, -27.76) * mm, v(-3.64, -28.15) * mm, v(-4.26, -28.5) * mm, v(-4.5, -28.55) * mm]});
            skFitSpline(sketch, "E275", {"points": [v(-4.5, -28.55) * mm, v(-4.74, -28.6) * mm, v(-5.08, -28.75) * mm, v(-5.25, -28.88) * mm]});
            skFitSpline(sketch, "E276", {"points": [v(-5.25, -28.88) * mm, v(-5.73, -29.25) * mm, v(-8.18, -29.4) * mm, v(-8.76, -29.1) * mm]});
            skFitSpline(sketch, "E277", {"points": [v(-8.76, -29.1) * mm, v(-9, -28.97) * mm, v(-9.36, -28.87) * mm, v(-9.56, -28.87) * mm]});
            skFitSpline(sketch, "E278", {"points": [v(-9.56, -28.87) * mm, v(-10.03, -28.87) * mm, v(-11.73, -28.08) * mm, v(-11.83, -27.81) * mm]});
            skFitSpline(sketch, "E279", {"points": [v(-11.83, -27.81) * mm, v(-11.87, -27.7) * mm, v(-12.08, -27.51) * mm, v(-12.3, -27.4) * mm]});
            skFitSpline(sketch, "E280", {"points": [v(-12.3, -27.4) * mm, v(-12.59, -27.25) * mm, v(-12.7, -27.07) * mm, v(-12.75, -26.63) * mm]});
            skFitSpline(sketch, "E281", {"points": [v(-12.75, -26.63) * mm, v(-12.83, -26.07) * mm, v(-13.44, -25.09) * mm, v(-13.71, -25.09) * mm]});
            skFitSpline(sketch, "E282", {"points": [v(-13.71, -25.09) * mm, v(-13.8, -25.09) * mm, v(-14.18, -25.4) * mm, v(-14.58, -25.77) * mm]});
            skFitSpline(sketch, "E283", {"points": [v(-14.58, -25.77) * mm, v(-15.32, -26.47) * mm, v(-16.31, -27.15) * mm, v(-17.19, -27.55) * mm]});
            skFitSpline(sketch, "E284", {"points": [v(-17.19, -27.55) * mm, v(-17.45, -27.67) * mm, v(-17.75, -27.86) * mm, v(-17.86, -27.97) * mm]});
            skFitSpline(sketch, "E285", {"points": [v(-17.86, -27.97) * mm, v(-17.97, -28.07) * mm, v(-18.29, -28.2) * mm, v(-18.57, -28.26) * mm]});
            skFitSpline(sketch, "E286", {"points": [v(-18.57, -28.26) * mm, v(-18.86, -28.3) * mm, v(-19.25, -28.46) * mm, v(-19.45, -28.6) * mm]});
            skFitSpline(sketch, "E287", {"points": [v(-19.45, -28.6) * mm, v(-19.93, -28.93) * mm, v(-21.4, -29.15) * mm, v(-23.72, -29.22) * mm]});
            skLineSegment(sketch, "E288", {"start": v(-32.15, -20.26) * mm, "end": v(-31.87, -23.66) * mm});
            skFitSpline(sketch, "E289", {"points": [v(-3.86, -26.65) * mm, v(-3.3, -26.43) * mm, v(-2.42, -25.46) * mm, v(-1.75, -24.3) * mm]});
            skFitSpline(sketch, "E290", {"points": [v(-1.75, -24.3) * mm, v(-0.99, -22.98) * mm, v(-0.1, -21.12) * mm, v(-0.1, -20.85) * mm]});
            skFitSpline(sketch, "E291", {"points": [v(-0.1, -20.85) * mm, v(-0.1, -20.74) * mm, v(-0.04, -20.6) * mm, v(0.02, -20.52) * mm]});
            skFitSpline(sketch, "E292", {"points": [v(0.02, -20.52) * mm, v(0.09, -20.45) * mm, v(0.38, -19.76) * mm, v(0.67, -18.99) * mm]});
            skFitSpline(sketch, "E293", {"points": [v(0.67, -18.99) * mm, v(0.95, -18.22) * mm, v(1.3, -17.27) * mm, v(1.46, -16.88) * mm]});
            skFitSpline(sketch, "E294", {"points": [v(1.46, -16.88) * mm, v(1.77, -16.05) * mm, v(1.83, -14.2) * mm, v(1.54, -13.82) * mm]});
            skFitSpline(sketch, "E295", {"points": [v(1.54, -13.82) * mm, v(1.24, -13.4) * mm, v(0.3, -13.37) * mm, v(-0.46, -13.75) * mm]});
            skFitSpline(sketch, "E296", {"points": [v(-0.46, -13.75) * mm, v(-1.78, -14.41) * mm, v(-3.69, -16.8) * mm, v(-4.81, -19.2) * mm]});
            skFitSpline(sketch, "E297", {"points": [v(-4.81, -19.2) * mm, v(-5, -19.62) * mm, v(-5.3, -20.22) * mm, v(-5.44, -20.53) * mm]});
            skFitSpline(sketch, "E298", {"points": [v(-5.44, -20.53) * mm, v(-5.59, -20.84) * mm, v(-5.7, -21.25) * mm, v(-5.7, -21.44) * mm]});
            skFitSpline(sketch, "E299", {"points": [v(-5.7, -21.44) * mm, v(-5.7, -21.63) * mm, v(-5.8, -22.05) * mm, v(-5.93, -22.38) * mm]});
            skFitSpline(sketch, "E300", {"points": [v(-5.93, -22.38) * mm, v(-6.25, -23.2) * mm, v(-6.04, -26.05) * mm, v(-5.64, -26.49) * mm]});
            skFitSpline(sketch, "E301", {"points": [v(-5.64, -26.49) * mm, v(-5.36, -26.8) * mm, v(-4.46, -26.87) * mm, v(-3.86, -26.65) * mm]});
            skLineSegment(sketch, "E302", {"start": v(-26.74, -28.83) * mm, "end": v(-23.72, -29.22) * mm});
            skFitSpline(sketch, "E303", {"points": [v(-10.54, -19.06) * mm, v(-10.5, -18.98) * mm, v(-10.52, -18.92) * mm, v(-10.6, -18.92) * mm]});
            skFitSpline(sketch, "E304", {"points": [v(-10.6, -18.92) * mm, v(-10.69, -18.92) * mm, v(-10.75, -18.98) * mm, v(-10.75, -19.06) * mm]});
            skFitSpline(sketch, "E305", {"points": [v(-10.75, -19.06) * mm, v(-10.75, -19.14) * mm, v(-10.73, -19.2) * mm, v(-10.7, -19.2) * mm]});
            skFitSpline(sketch, "E306", {"points": [v(-10.7, -19.2) * mm, v(-10.66, -19.2) * mm, v(-10.6, -19.14) * mm, v(-10.54, -19.06) * mm]});
            skFitSpline(sketch, "E307", {"points": [v(-9.94, -18.23) * mm, v(-9.9, -18.12) * mm, v(-9.96, -18.07) * mm, v(-10.06, -18.1) * mm]});
            skFitSpline(sketch, "E308", {"points": [v(-10.06, -18.1) * mm, v(-10.16, -18.14) * mm, v(-10.27, -18.25) * mm, v(-10.3, -18.35) * mm]});
            skFitSpline(sketch, "E309", {"points": [v(-10.3, -18.35) * mm, v(-10.34, -18.46) * mm, v(-10.29, -18.5) * mm, v(-10.18, -18.47) * mm]});
            skFitSpline(sketch, "E310", {"points": [v(-10.18, -18.47) * mm, v(-10.08, -18.44) * mm, v(-9.97, -18.33) * mm, v(-9.94, -18.23) * mm]});
            skFitSpline(sketch, "E311", {"points": [v(-30.3, -17.97) * mm, v(-29.34, -15.08) * mm, v(-27.83, -12.44) * mm, v(-25.44, -9.52) * mm]});
            skFitSpline(sketch, "E312", {"points": [v(-25.44, -9.52) * mm, v(-24.92, -8.88) * mm, v(-24.52, -8.33) * mm, v(-24.55, -8.3) * mm]});
            skFitSpline(sketch, "E313", {"points": [v(-24.55, -8.3) * mm, v(-24.94, -7.91) * mm, v(-29.12, -12.3) * mm, v(-29.12, -13.08) * mm]});
            skFitSpline(sketch, "E314", {"points": [v(-29.12, -13.08) * mm, v(-29.12, -13.19) * mm, v(-29.25, -13.43) * mm, v(-29.4, -13.63) * mm]});
            skFitSpline(sketch, "E315", {"points": [v(-29.4, -13.63) * mm, v(-29.55, -13.83) * mm, v(-29.68, -14.07) * mm, v(-29.68, -14.18) * mm]});
            skFitSpline(sketch, "E316", {"points": [v(-29.68, -14.18) * mm, v(-29.68, -14.29) * mm, v(-29.74, -14.44) * mm, v(-29.8, -14.51) * mm]});
            skFitSpline(sketch, "E317", {"points": [v(-29.8, -14.51) * mm, v(-30.02, -14.74) * mm, v(-30.66, -17.14) * mm, v(-30.66, -17.7) * mm]});
            skFitSpline(sketch, "E318", {"points": [v(-30.66, -17.7) * mm, v(-30.66, -18.23) * mm, v(-30.43, -18.4) * mm, v(-30.3, -17.97) * mm]});
            skFitSpline(sketch, "E319", {"points": [v(-7.88, -16.23) * mm, v(-7.5, -15.87) * mm, v(-6.85, -15.32) * mm, v(-6.44, -15) * mm]});
            skFitSpline(sketch, "E320", {"points": [v(-6.44, -15) * mm, v(-5.68, -14.4) * mm, v(-5.53, -14.15) * mm, v(-5.95, -14.16) * mm]});
            skFitSpline(sketch, "E321", {"points": [v(-5.95, -14.16) * mm, v(-6.24, -14.16) * mm, v(-6.44, -14.3) * mm, v(-7.58, -15.3) * mm]});
            skFitSpline(sketch, "E322", {"points": [v(-7.58, -15.3) * mm, v(-9.02, -16.58) * mm, v(-9.63, -17.25) * mm, v(-9.63, -17.56) * mm]});
            skFitSpline(sketch, "E323", {"points": [v(-9.63, -17.56) * mm, v(-9.63, -17.88) * mm, v(-9.72, -17.95) * mm, v(-7.88, -16.23) * mm]});
            skFitSpline(sketch, "E324", {"points": [v(1.93, -9.94) * mm, v(1.7, -9.86) * mm, v(1.04, -9.75) * mm, v(0.46, -9.68) * mm]});
            skFitSpline(sketch, "E325", {"points": [v(0.46, -9.68) * mm, v(-0.93, -9.5) * mm, v(-2.1, -9.2) * mm, v(-2.66, -8.84) * mm]});
            skFitSpline(sketch, "E326", {"points": [v(-2.66, -8.84) * mm, v(-2.9, -8.68) * mm, v(-3.4, -8.4) * mm, v(-3.74, -8.21) * mm]});
            skFitSpline(sketch, "E327", {"points": [v(-3.74, -8.21) * mm, v(-4.84, -7.61) * mm, v(-7.15, -4.96) * mm, v(-8.02, -3.29) * mm]});
            skFitSpline(sketch, "E328", {"points": [v(-8.02, -3.29) * mm, v(-8.15, -3.04) * mm, v(-8.31, -3) * mm, v(-9.43, -3) * mm]});
            skFitSpline(sketch, "E329", {"points": [v(-9.43, -3) * mm, v(-10.8, -3) * mm, v(-11.94, -2.78) * mm, v(-12.74, -2.36) * mm]});
            skFitSpline(sketch, "E330", {"points": [v(-12.74, -2.36) * mm, v(-13.03, -2.22) * mm, v(-13.35, -2.1) * mm, v(-13.46, -2.1) * mm]});
            skFitSpline(sketch, "E331", {"points": [v(-13.46, -2.1) * mm, v(-13.57, -2.1) * mm, v(-13.74, -2) * mm, v(-13.84, -1.89) * mm]});
            skFitSpline(sketch, "E332", {"points": [v(-13.84, -1.89) * mm, v(-13.93, -1.77) * mm, v(-14.11, -1.68) * mm, v(-14.23, -1.68) * mm]});
            skFitSpline(sketch, "E333", {"points": [v(-14.23, -1.68) * mm, v(-14.95, -1.68) * mm, v(-17.64, 0.8) * mm, v(-18, 1.78) * mm]});
            skFitSpline(sketch, "E334", {"points": [v(-18.71, 8.94) * mm, v(-18.6, 9.41) * mm, v(-18.42, 9.64) * mm, v(-17.85, 10.08) * mm]});
            skFitSpline(sketch, "E335", {"points": [v(-17.85, 10.08) * mm, v(-17.45, 10.38) * mm, v(-16.97, 10.67) * mm, v(-16.78, 10.73) * mm]});
            skFitSpline(sketch, "E336", {"points": [v(-16.78, 10.73) * mm, v(-16.59, 10.78) * mm, v(-16.27, 10.93) * mm, v(-16.08, 11.06) * mm]});
            skFitSpline(sketch, "E337", {"points": [v(-16.08, 11.06) * mm, v(-15.89, 11.19) * mm, v(-15.23, 11.36) * mm, v(-14.6, 11.45) * mm]});
            skFitSpline(sketch, "E338", {"points": [v(-14.6, 11.45) * mm, v(-13.6, 11.6) * mm, v(-13.44, 11.59) * mm, v(-12.96, 11.35) * mm]});
            skFitSpline(sketch, "E339", {"points": [v(-12.96, 11.35) * mm, v(-12.37, 11.05) * mm, v(-11.79, 11) * mm, v(-11.7, 11.24) * mm]});
            skFitSpline(sketch, "E340", {"points": [v(-11.7, 11.24) * mm, v(-11.68, 11.32) * mm, v(-11.68, 11.61) * mm, v(-11.71, 11.88) * mm]});
            skFitSpline(sketch, "E341", {"points": [v(-11.71, 11.88) * mm, v(-11.79, 12.53) * mm, v(-12.06, 12.6) * mm, v(-13.77, 12.46) * mm]});
            skFitSpline(sketch, "E342", {"points": [v(-13.77, 12.46) * mm, v(-14.54, 12.4) * mm, v(-16.68, 12.38) * mm, v(-18.53, 12.42) * mm]});
            skFitSpline(sketch, "E343", {"points": [v(-18.53, 12.42) * mm, v(-21.67, 12.5) * mm, v(-24.34, 12.4) * mm, v(-28.77, 12.05) * mm]});
            skFitSpline(sketch, "E344", {"points": [v(-28.77, 12.05) * mm, v(-29.77, 11.98) * mm, v(-34.82, 11.85) * mm, v(-39.98, 11.78) * mm]});
            skFitSpline(sketch, "E345", {"points": [v(-39.98, 11.78) * mm, v(-47.12, 11.68) * mm, v(-49.7, 11.6) * mm, v(-50.7, 11.44) * mm]});
            skFitSpline(sketch, "E346", {"points": [v(-50.7, 11.44) * mm, v(-52.42, 11.17) * mm, v(-52.58, 11.17) * mm, v(-52.96, 11.48) * mm]});
            skFitSpline(sketch, "E347", {"points": [v(-48.27, 38.42) * mm, v(-47.72, 38.42) * mm, v(-44.66, 38.26) * mm, v(-41.46, 38.06) * mm]});
            skFitSpline(sketch, "E348", {"points": [v(-41.46, 38.06) * mm, v(-38.26, 37.87) * mm, v(-33.97, 37.62) * mm, v(-31.92, 37.5) * mm]});
            skFitSpline(sketch, "E349", {"points": [v(-31.92, 37.5) * mm, v(-29.88, 37.4) * mm, v(-27.86, 37.27) * mm, v(-27.44, 37.23) * mm]});
            skFitSpline(sketch, "E350", {"points": [v(-27.44, 37.23) * mm, v(-27.01, 37.2) * mm, v(-26.04, 37.13) * mm, v(-25.26, 37.1) * mm]});
            skFitSpline(sketch, "E351", {"points": [v(-25.26, 37.1) * mm, v(-24.5, 37.05) * mm, v(-21.75, 36.9) * mm, v(-19.17, 36.74) * mm]});
            skFitSpline(sketch, "E352", {"points": [v(-19.17, 36.74) * mm, v(-13.13, 36.37) * mm, v(-9.68, 36.18) * mm, v(-9.11, 36.18) * mm]});
            skFitSpline(sketch, "E353", {"points": [v(-9.11, 36.18) * mm, v(-8.7, 36.18) * mm, v(-8.67, 36.2) * mm, v(-8.78, 36.5) * mm]});
            skFitSpline(sketch, "E354", {"points": [v(-8.78, 36.5) * mm, v(-8.9, 36.81) * mm, v(-8.77, 38.05) * mm, v(-8.53, 39) * mm]});
            skFitSpline(sketch, "E355", {"points": [v(-8.53, 39) * mm, v(-8.36, 39.69) * mm, v(-8.01, 40.16) * mm, v(-6.87, 41.23) * mm]});
            skFitSpline(sketch, "E356", {"points": [v(-6.87, 41.23) * mm, v(-5.3, 42.72) * mm, v(-2.93, 43.74) * mm, v(0.6, 44.46) * mm]});
            skFitSpline(sketch, "E357", {"points": [v(0.6, 44.46) * mm, v(3.93, 45.14) * mm, v(7.18, 45.4) * mm, v(9.36, 45.17) * mm]});
            skFitSpline(sketch, "E358", {"points": [v(9.36, 45.17) * mm, v(13.69, 44.7) * mm, v(15.6, 44) * mm, v(16.2, 42.67) * mm]});
            skFitSpline(sketch, "E359", {"points": [v(16.2, 42.67) * mm, v(16.57, 41.8) * mm, v(16.46, 40.97) * mm, v(15.85, 40.16) * mm]});
            skFitSpline(sketch, "E360", {"points": [v(15.85, 40.16) * mm, v(15.33, 39.47) * mm, v(14.44, 39.04) * mm, v(12.52, 38.56) * mm]});
            skFitSpline(sketch, "E361", {"points": [v(12.52, 38.56) * mm, v(11.43, 38.28) * mm, v(11.23, 38.27) * mm, v(10.14, 38.42) * mm]});
            skFitSpline(sketch, "E362", {"points": [v(10.14, 38.42) * mm, v(8.9, 38.6) * mm, v(7.07, 39.14) * mm, v(6.53, 39.48) * mm]});
            skFitSpline(sketch, "E363", {"points": [v(6.53, 39.48) * mm, v(6.36, 39.6) * mm, v(6.15, 39.8) * mm, v(6.07, 39.96) * mm]});
            skFitSpline(sketch, "E364", {"points": [v(6.07, 39.96) * mm, v(5.82, 40.43) * mm, v(6.27, 40.53) * mm, v(7.57, 40.28) * mm]});
            skFitSpline(sketch, "E365", {"points": [v(7.57, 40.28) * mm, v(8.66, 40.07) * mm, v(8.76, 40.07) * mm, v(9.67, 40.33) * mm]});
            skFitSpline(sketch, "E366", {"points": [v(9.67, 40.33) * mm, v(10.56, 40.59) * mm, v(10.62, 40.63) * mm, v(10.72, 41.09) * mm]});
            skFitSpline(sketch, "E367", {"points": [v(10.72, 41.09) * mm, v(10.92, 42) * mm, v(10.01, 42.72) * mm, v(8.07, 43.2) * mm]});
            skFitSpline(sketch, "E368", {"points": [v(8.07, 43.2) * mm, v(7.12, 43.44) * mm, v(6.78, 43.46) * mm, v(5.13, 43.34) * mm]});
            skFitSpline(sketch, "E369", {"points": [v(5.13, 43.34) * mm, v(3.05, 43.2) * mm, v(2.71, 43.06) * mm, v(1.82, 42.07) * mm]});
            skFitSpline(sketch, "E370", {"points": [v(1.82, 42.07) * mm, v(1.14, 41.32) * mm, v(0.88, 40.78) * mm, v(0.88, 40.1) * mm]});
            skFitSpline(sketch, "E371", {"points": [v(0.88, 40.1) * mm, v(0.88, 39.36) * mm, v(1.13, 39) * mm, v(2.36, 38) * mm]});
            skFitSpline(sketch, "E372", {"points": [v(2.36, 38) * mm, v(3.52, 37.06) * mm, v(3.94, 36.83) * mm, v(5.78, 36.1) * mm]});
            skFitSpline(sketch, "E373", {"points": [v(5.78, 36.1) * mm, v(7.3, 35.51) * mm, v(5.96, 35.53) * mm, v(16.37, 36.01) * mm]});
            skFitSpline(sketch, "E374", {"points": [v(16.37, 36.01) * mm, v(25.87, 36.45) * mm, v(28.47, 36.57) * mm, v(38.24, 37.02) * mm]});
            skFitSpline(sketch, "E375", {"points": [v(38.24, 37.02) * mm, v(43.18, 37.25) * mm, v(50.1, 37.57) * mm, v(53.64, 37.74) * mm]});
            skFitSpline(sketch, "E376", {"points": [v(53.64, 37.74) * mm, v(57.17, 37.9) * mm, v(60.1, 38) * mm, v(60.13, 37.96) * mm]});
            skFitSpline(sketch, "E377", {"points": [v(60.13, 37.96) * mm, v(60.17, 37.92) * mm, v(60.14, 37.77) * mm, v(60.07, 37.63) * mm]});
            skFitSpline(sketch, "E378", {"points": [v(60.07, 37.63) * mm, v(60, 37.49) * mm, v(59.8, 37.02) * mm, v(59.65, 36.6) * mm]});
            skFitSpline(sketch, "E379", {"points": [v(59.65, 36.6) * mm, v(59.22, 35.46) * mm, v(56.91, 29.54) * mm, v(56.03, 27.3) * mm]});
            skLineSegment(sketch, "E380", {"start": v(-52.96, 11.48) * mm, "end": v(-53.27, 11.73) * mm});
            skLineSegment(sketch, "E381", {"start": v(-53.27, 11.73) * mm, "end": v(-49.67, 18.65) * mm});
            skLineSegment(sketch, "E382", {"start": v(-49.67, 18.65) * mm, "end": v(-46.06, 25.56) * mm});
            skLineSegment(sketch, "E383", {"start": v(-46.06, 25.56) * mm, "end": v(-47.67, 31.99) * mm});
            skLineSegment(sketch, "E384", {"start": v(-47.67, 31.99) * mm, "end": v(-49.27, 38.42) * mm});
            skLineSegment(sketch, "E385", {"start": v(-49.27, 38.42) * mm, "end": v(-48.27, 38.42) * mm});
            skFitSpline(sketch, "E386", {"points": [v(56.52, 22.75) * mm, v(57.21, 21.3) * mm, v(58.5, 18.62) * mm, v(59.4, 16.78) * mm]});
            skFitSpline(sketch, "E387", {"points": [v(59.4, 16.78) * mm, v(60.3, 14.94) * mm, v(61.03, 13.36) * mm, v(61.03, 13.27) * mm]});
            skFitSpline(sketch, "E388", {"points": [v(61.03, 13.27) * mm, v(61.03, 12.87) * mm, v(60.64, 12.36) * mm, v(59.93, 11.81) * mm]});
            skFitSpline(sketch, "E389", {"points": [v(59.93, 11.81) * mm, v(59.35, 11.37) * mm, v(59.04, 11.22) * mm, v(58.66, 11.22) * mm]});
            skFitSpline(sketch, "E390", {"points": [v(58.66, 11.22) * mm, v(58.38, 11.23) * mm, v(54.34, 11.35) * mm, v(49.67, 11.5) * mm]});
            skFitSpline(sketch, "E391", {"points": [v(49.67, 11.5) * mm, v(45, 11.65) * mm, v(38.1, 11.87) * mm, v(34.32, 11.98) * mm]});
            skFitSpline(sketch, "E392", {"points": [v(34.32, 11.98) * mm, v(30.54, 12.1) * mm, v(26.4, 12.23) * mm, v(25.12, 12.28) * mm]});
            skLineSegment(sketch, "E393", {"start": v(56.03, 27.3) * mm, "end": v(55.26, 25.38) * mm});
            skLineSegment(sketch, "E394", {"start": v(55.26, 25.38) * mm, "end": v(56.52, 22.75) * mm});
            skFitSpline(sketch, "E395", {"points": [v(22.76, 10.61) * mm, v(22.75, 9.34) * mm, v(22.68, 8.74) * mm, v(22.52, 8.42) * mm]});
            skFitSpline(sketch, "E396", {"points": [v(22.52, 8.42) * mm, v(22.4, 8.17) * mm, v(22.33, 7.79) * mm, v(22.37, 7.53) * mm]});
            skFitSpline(sketch, "E397", {"points": [v(22.37, 7.53) * mm, v(22.4, 7.28) * mm, v(22.35, 6.9) * mm, v(22.22, 6.67) * mm]});
            skFitSpline(sketch, "E398", {"points": [v(22.22, 6.67) * mm, v(22.1, 6.43) * mm, v(21.96, 6) * mm, v(21.9, 5.68) * mm]});
            skFitSpline(sketch, "E399", {"points": [v(21.9, 5.68) * mm, v(21.78, 5.01) * mm, v(21.43, 4) * mm, v(21.14, 3.49) * mm]});
            skFitSpline(sketch, "E400", {"points": [v(21.14, 3.49) * mm, v(21.02, 3.29) * mm, v(20.93, 3.02) * mm, v(20.93, 2.9) * mm]});
            skFitSpline(sketch, "E401", {"points": [v(20.93, 2.9) * mm, v(20.93, 2.7) * mm, v(20, 0.8) * mm, v(18.9, -1.18) * mm]});
            skFitSpline(sketch, "E402", {"points": [v(18.9, -1.18) * mm, v(18.7, -1.56) * mm, v(18.25, -2.24) * mm, v(17.9, -2.68) * mm]});
            skFitSpline(sketch, "E403", {"points": [v(17.9, -2.68) * mm, v(17.56, -3.13) * mm, v(17, -3.88) * mm, v(16.64, -4.34) * mm]});
            skFitSpline(sketch, "E404", {"points": [v(16.64, -4.34) * mm, v(15.64, -5.66) * mm, v(13.14, -8.12) * mm, v(12.62, -8.3) * mm]});
            skFitSpline(sketch, "E405", {"points": [v(12.62, -8.3) * mm, v(12.37, -8.38) * mm, v(12.07, -8.53) * mm, v(11.96, -8.62) * mm]});
            skFitSpline(sketch, "E406", {"points": [v(11.96, -8.62) * mm, v(11.84, -8.72) * mm, v(11.34, -8.9) * mm, v(10.84, -9.04) * mm]});
            skFitSpline(sketch, "E407", {"points": [v(10.84, -9.04) * mm, v(10.34, -9.16) * mm, v(9.77, -9.35) * mm, v(9.57, -9.46) * mm]});
            skFitSpline(sketch, "E408", {"points": [v(9.57, -9.46) * mm, v(8.87, -9.82) * mm, v(2.75, -10.2) * mm, v(1.93, -9.94) * mm]});
            skLineSegment(sketch, "E409", {"start": v(25.12, 12.28) * mm, "end": v(22.78, 12.37) * mm});
            skLineSegment(sketch, "E410", {"start": v(22.78, 12.37) * mm, "end": v(22.76, 10.61) * mm});
            skFitSpline(sketch, "E411", {"points": [v(-9.54, 0.22) * mm, v(-9.5, 0.34) * mm, v(-9.55, 0.55) * mm, v(-9.67, 0.68) * mm]});
            skFitSpline(sketch, "E412", {"points": [v(-9.67, 0.68) * mm, v(-9.8, 0.8) * mm, v(-9.93, 1.3) * mm, v(-9.99, 1.76) * mm]});
            skFitSpline(sketch, "E413", {"points": [v(-9.99, 1.76) * mm, v(-10.04, 2.22) * mm, v(-10.2, 2.82) * mm, v(-10.34, 3.1) * mm]});
            skFitSpline(sketch, "E414", {"points": [v(-10.34, 3.1) * mm, v(-10.61, 3.62) * mm, v(-10.9, 5.22) * mm, v(-10.9, 6.23) * mm]});
            skFitSpline(sketch, "E415", {"points": [v(-10.9, 6.23) * mm, v(-10.9, 7.1) * mm, v(-11.35, 7.64) * mm, v(-12.06, 7.62) * mm]});
            skFitSpline(sketch, "E416", {"points": [v(-12.06, 7.62) * mm, v(-12.85, 7.6) * mm, v(-13.58, 7.16) * mm, v(-14.08, 6.4) * mm]});
            skFitSpline(sketch, "E417", {"points": [v(-14.08, 6.4) * mm, v(-14.51, 5.76) * mm, v(-14.54, 5.65) * mm, v(-14.54, 4.47) * mm]});
            skFitSpline(sketch, "E418", {"points": [v(-14.54, 4.47) * mm, v(-14.54, 3.65) * mm, v(-14.47, 3.08) * mm, v(-14.34, 2.82) * mm]});
            skFitSpline(sketch, "E419", {"points": [v(-14.34, 2.82) * mm, v(-14.1, 2.39) * mm, v(-12.56, 0.99) * mm, v(-12.3, 0.99) * mm]});
            skFitSpline(sketch, "E420", {"points": [v(-12.3, 0.99) * mm, v(-12.15, 0.99) * mm, v(-11.85, 0.85) * mm, v(-10.68, 0.25) * mm]});
            skFitSpline(sketch, "E421", {"points": [v(-10.68, 0.25) * mm, v(-10.13, -0.04) * mm, v(-9.64, -0.05) * mm, v(-9.54, 0.22) * mm]});
            skLineSegment(sketch, "E422", {"start": v(1.93, -9.94) * mm, "end": v(1.93, -9.94) * mm});
            skFitSpline(sketch, "E423", {"points": [v(15.04, 13.58) * mm, v(16.72, 13.73) * mm, v(18.19, 14.07) * mm, v(18.35, 14.34) * mm]});
            skFitSpline(sketch, "E424", {"points": [v(18.35, 14.34) * mm, v(18.68, 14.86) * mm, v(17.67, 15.75) * mm, v(16.16, 16.27) * mm]});
            skFitSpline(sketch, "E425", {"points": [v(16.16, 16.27) * mm, v(15.32, 16.56) * mm, v(14.85, 16.6) * mm, v(10.2, 16.71) * mm]});
            skFitSpline(sketch, "E426", {"points": [v(10.2, 16.71) * mm, v(6.56, 16.8) * mm, v(4.79, 16.8) * mm, v(3.83, 16.68) * mm]});
            skFitSpline(sketch, "E427", {"points": [v(3.83, 16.68) * mm, v(3.1, 16.6) * mm, v(1.33, 16.53) * mm, v(-0.1, 16.55) * mm]});
            skFitSpline(sketch, "E428", {"points": [v(-0.1, 16.55) * mm, v(-3.01, 16.58) * mm, v(-6.44, 16.38) * mm, v(-7.38, 16.13) * mm]});
            skFitSpline(sketch, "E429", {"points": [v(-7.38, 16.13) * mm, v(-8.04, 15.95) * mm, v(-8.65, 15.61) * mm, v(-8.65, 15.41) * mm]});
            skFitSpline(sketch, "E430", {"points": [v(-8.65, 15.41) * mm, v(-8.65, 15.35) * mm, v(-8.5, 15.25) * mm, v(-8.3, 15.2) * mm]});
            skFitSpline(sketch, "E431", {"points": [v(-8.3, 15.2) * mm, v(-8.1, 15.16) * mm, v(-7.95, 15.07) * mm, v(-7.95, 15) * mm]});
            skFitSpline(sketch, "E432", {"points": [v(-7.95, 15) * mm, v(-7.95, 14.83) * mm, v(-5.4, 14.04) * mm, v(-3.4, 13.6) * mm]});
            skFitSpline(sketch, "E433", {"points": [v(-3.4, 13.6) * mm, v(-2.38, 13.37) * mm, v(-1.5, 13.35) * mm, v(5.5, 13.38) * mm]});
            skFitSpline(sketch, "E434", {"points": [v(5.5, 13.38) * mm, v(9.97, 13.4) * mm, v(14.03, 13.48) * mm, v(15.04, 13.58) * mm]});
            skFitSpline(sketch, "E435", {"points": [v(55.36, 13.85) * mm, v(55.6, 14.1) * mm, v(55.61, 14.37) * mm, v(55.39, 14.77) * mm]});
            skFitSpline(sketch, "E436", {"points": [v(55.39, 14.77) * mm, v(55.3, 14.94) * mm, v(55.08, 15.46) * mm, v(54.9, 15.92) * mm]});
            skFitSpline(sketch, "E437", {"points": [v(54.9, 15.92) * mm, v(54.74, 16.38) * mm, v(54.28, 17.64) * mm, v(53.88, 18.72) * mm]});
            skFitSpline(sketch, "E438", {"points": [v(53.88, 18.72) * mm, v(52.85, 21.54) * mm, v(52.53, 22.53) * mm, v(52.33, 23.51) * mm]});
            skFitSpline(sketch, "E439", {"points": [v(52.33, 23.51) * mm, v(52.13, 24.54) * mm, v(52.22, 26.63) * mm, v(52.54, 28.26) * mm]});
            skFitSpline(sketch, "E440", {"points": [v(52.54, 28.26) * mm, v(53, 30.6) * mm, v(53.35, 34.65) * mm, v(53.12, 34.88) * mm]});
            skFitSpline(sketch, "E441", {"points": [v(53.12, 34.88) * mm, v(52.96, 35.04) * mm, v(45.07, 34.86) * mm, v(42.45, 34.64) * mm]});
            skFitSpline(sketch, "E442", {"points": [v(42.45, 34.64) * mm, v(41.52, 34.56) * mm, v(38.97, 34.5) * mm, v(36.77, 34.5) * mm]});
            skFitSpline(sketch, "E443", {"points": [v(36.77, 34.5) * mm, v(32.7, 34.49) * mm, v(28.96, 34.34) * mm, v(25.84, 34.08) * mm]});
            skFitSpline(sketch, "E444", {"points": [v(25.84, 34.08) * mm, v(21.23, 33.68) * mm, v(18.22, 33.51) * mm, v(15.7, 33.51) * mm]});
            skFitSpline(sketch, "E445", {"points": [v(13.77, 32.45) * mm, v(14.92, 31) * mm, v(15.21, 30.17) * mm, v(15.07, 28.84) * mm]});
            skFitSpline(sketch, "E446", {"points": [v(15.07, 28.84) * mm, v(14.97, 27.9) * mm, v(14.9, 27.75) * mm, v(14.16, 26.77) * mm]});
            skFitSpline(sketch, "E447", {"points": [v(14.16, 26.77) * mm, v(13.73, 26.18) * mm, v(13.13, 25.54) * mm, v(12.84, 25.35) * mm]});
            skFitSpline(sketch, "E448", {"points": [v(12.84, 25.35) * mm, v(11.02, 24.12) * mm, v(8.82, 22.9) * mm, v(7.66, 22.5) * mm]});
            skFitSpline(sketch, "E449", {"points": [v(7.66, 22.5) * mm, v(6.93, 22.25) * mm, v(6.26, 21.98) * mm, v(6.17, 21.9) * mm]});
            skFitSpline(sketch, "E450", {"points": [v(6.17, 21.9) * mm, v(6.08, 21.83) * mm, v(5.8, 21.67) * mm, v(5.55, 21.54) * mm]});
            skFitSpline(sketch, "E451", {"points": [v(5.55, 21.54) * mm, v(5.3, 21.42) * mm, v(4.87, 20.97) * mm, v(4.59, 20.54) * mm]});
            skFitSpline(sketch, "E452", {"points": [v(4.59, 20.54) * mm, v(4.12, 19.84) * mm, v(4.08, 19.7) * mm, v(4.16, 19.11) * mm]});
            skFitSpline(sketch, "E453", {"points": [v(4.16, 19.11) * mm, v(4.2, 18.76) * mm, v(4.27, 18.44) * mm, v(4.3, 18.4) * mm]});
            skFitSpline(sketch, "E454", {"points": [v(4.3, 18.4) * mm, v(4.4, 18.32) * mm, v(6.6, 18.3) * mm, v(8.45, 18.36) * mm]});
            skFitSpline(sketch, "E455", {"points": [v(8.45, 18.36) * mm, v(10.2, 18.42) * mm, v(13.54, 18.18) * mm, v(15.11, 17.88) * mm]});
            skFitSpline(sketch, "E456", {"points": [v(15.11, 17.88) * mm, v(15.65, 17.78) * mm, v(16.66, 17.62) * mm, v(17.36, 17.53) * mm]});
            skFitSpline(sketch, "E457", {"points": [v(17.36, 17.53) * mm, v(18.73, 17.35) * mm, v(19.95, 17) * mm, v(21.16, 16.45) * mm]});
            skFitSpline(sketch, "E458", {"points": [v(21.16, 16.45) * mm, v(21.72, 16.2) * mm, v(22.07, 15.91) * mm, v(22.42, 15.43) * mm]});
            skFitSpline(sketch, "E459", {"points": [v(22.42, 15.43) * mm, v(22.68, 15.06) * mm, v(23, 14.71) * mm, v(23.14, 14.66) * mm]});
            skFitSpline(sketch, "E460", {"points": [v(23.14, 14.66) * mm, v(23.51, 14.52) * mm, v(26.85, 14.37) * mm, v(28.57, 14.42) * mm]});
            skFitSpline(sketch, "E461", {"points": [v(28.57, 14.42) * mm, v(31.9, 14.53) * mm, v(37.95, 14.4) * mm, v(40.9, 14.17) * mm]});
            skFitSpline(sketch, "E462", {"points": [v(40.9, 14.17) * mm, v(42.06, 14.08) * mm, v(44.93, 13.97) * mm, v(47.27, 13.94) * mm]});
            skFitSpline(sketch, "E463", {"points": [v(47.27, 13.94) * mm, v(49.6, 13.9) * mm, v(51.78, 13.82) * mm, v(52.1, 13.76) * mm]});
            skFitSpline(sketch, "E464", {"points": [v(52.1, 13.76) * mm, v(53.1, 13.56) * mm, v(55.13, 13.62) * mm, v(55.36, 13.85) * mm]});
            skLineSegment(sketch, "E465", {"start": v(15.7, 33.51) * mm, "end": v(12.93, 33.51) * mm});
            skLineSegment(sketch, "E466", {"start": v(12.93, 33.51) * mm, "end": v(13.77, 32.45) * mm});
            skFitSpline(sketch, "E467", {"points": [v(17, 18.6) * mm, v(16.8, 18.82) * mm, v(16.76, 19.64) * mm, v(16.92, 19.9) * mm]});
            skFitSpline(sketch, "E468", {"points": [v(16.92, 19.9) * mm, v(16.97, 19.97) * mm, v(17.2, 20.07) * mm, v(17.42, 20.12) * mm]});
            skFitSpline(sketch, "E469", {"points": [v(17.42, 20.12) * mm, v(17.64, 20.17) * mm, v(17.9, 20.3) * mm, v(17.98, 20.4) * mm]});
            skFitSpline(sketch, "E470", {"points": [v(17.98, 20.4) * mm, v(18.08, 20.52) * mm, v(18.12, 21.75) * mm, v(18.1, 24.2) * mm]});
            skFitSpline(sketch, "E471", {"points": [v(17.57, 28) * mm, v(17.3, 28.08) * mm, v(17, 28.3) * mm, v(16.91, 28.48) * mm]});
            skFitSpline(sketch, "E472", {"points": [v(16.91, 28.48) * mm, v(16.69, 28.93) * mm, v(16.83, 29.56) * mm, v(17.2, 29.76) * mm]});
            skFitSpline(sketch, "E473", {"points": [v(17.2, 29.76) * mm, v(17.38, 29.86) * mm, v(18.63, 29.94) * mm, v(20.5, 29.98) * mm]});
            skFitSpline(sketch, "E474", {"points": [v(20.5, 29.98) * mm, v(23.63, 30.05) * mm, v(24.56, 29.95) * mm, v(25.57, 29.44) * mm]});
            skFitSpline(sketch, "E475", {"points": [v(25.57, 29.44) * mm, v(27.02, 28.7) * mm, v(27.48, 26.95) * mm, v(26.62, 25.43) * mm]});
            skLineSegment(sketch, "E476", {"start": v(18.1, 24.2) * mm, "end": v(18.06, 27.84) * mm});
            skLineSegment(sketch, "E477", {"start": v(18.06, 27.84) * mm, "end": v(17.57, 28) * mm});
            skFitSpline(sketch, "E478", {"points": [v(26.64, 24.52) * mm, v(27.5, 23.7) * mm, v(27.88, 22.08) * mm, v(27.47, 20.9) * mm]});
            skFitSpline(sketch, "E479", {"points": [v(27.47, 20.9) * mm, v(27.24, 20.25) * mm, v(27.25, 20.1) * mm, v(27.51, 20.26) * mm]});
            skFitSpline(sketch, "E480", {"points": [v(27.51, 20.26) * mm, v(27.76, 20.41) * mm, v(28.01, 20.99) * mm, v(29.48, 24.74) * mm]});
            skFitSpline(sketch, "E481", {"points": [v(29.48, 24.74) * mm, v(30.49, 27.3) * mm, v(30.88, 28.5) * mm, v(30.88, 28.93) * mm]});
            skFitSpline(sketch, "E482", {"points": [v(30.88, 28.93) * mm, v(30.88, 29.26) * mm, v(30.96, 29.6) * mm, v(31.05, 29.7) * mm]});
            skFitSpline(sketch, "E483", {"points": [v(31.05, 29.7) * mm, v(31.16, 29.8) * mm, v(31.73, 29.87) * mm, v(32.66, 29.87) * mm]});
            skFitSpline(sketch, "E484", {"points": [v(32.66, 29.87) * mm, v(33.87, 29.87) * mm, v(34.15, 29.83) * mm, v(34.36, 29.62) * mm]});
            skFitSpline(sketch, "E485", {"points": [v(34.36, 29.62) * mm, v(34.5, 29.48) * mm, v(35.3, 27.54) * mm, v(36.13, 25.3) * mm]});
            skFitSpline(sketch, "E486", {"points": [v(36.13, 25.3) * mm, v(38.01, 20.28) * mm, v(38.07, 20.16) * mm, v(38.57, 20.22) * mm]});
            skLineSegment(sketch, "E487", {"start": v(26.62, 25.43) * mm, "end": v(26.29, 24.84) * mm});
            skLineSegment(sketch, "E488", {"start": v(26.29, 24.84) * mm, "end": v(26.64, 24.52) * mm});
            skFitSpline(sketch, "E489", {"points": [v(38.52, 28.07) * mm, v(38.01, 28.2) * mm, v(37.75, 28.53) * mm, v(37.75, 29.04) * mm]});
            skFitSpline(sketch, "E490", {"points": [v(37.75, 29.04) * mm, v(37.75, 29.82) * mm, v(37.93, 29.87) * mm, v(40.9, 29.87) * mm]});
            skFitSpline(sketch, "E491", {"points": [v(40.9, 29.87) * mm, v(43.19, 29.87) * mm, v(43.66, 29.83) * mm, v(43.84, 29.65) * mm]});
            skFitSpline(sketch, "E492", {"points": [v(43.84, 29.65) * mm, v(44.33, 29.16) * mm, v(43.9, 28.05) * mm, v(43.23, 28.05) * mm]});
            skFitSpline(sketch, "E493", {"points": [v(43.23, 28.05) * mm, v(42.8, 28.05) * mm, v(42.66, 27.61) * mm, v(42.66, 26.3) * mm]});
            skLineSegment(sketch, "E494", {"start": v(38.57, 20.22) * mm, "end": v(38.95, 20.26) * mm});
            skLineSegment(sketch, "E495", {"start": v(38.95, 20.26) * mm, "end": v(38.95, 24.11) * mm});
            skLineSegment(sketch, "E496", {"start": v(38.95, 24.11) * mm, "end": v(38.95, 27.96) * mm});
            skLineSegment(sketch, "E497", {"start": v(38.95, 27.96) * mm, "end": v(38.52, 28.07) * mm});
            skFitSpline(sketch, "E498", {"points": [v(46.44, 26.4) * mm, v(46.44, 27.11) * mm, v(46.4, 27.76) * mm, v(46.34, 27.84) * mm]});
            skFitSpline(sketch, "E499", {"points": [v(46.34, 27.84) * mm, v(46.28, 27.93) * mm, v(46.02, 28.05) * mm, v(45.75, 28.13) * mm]});
            skFitSpline(sketch, "E500", {"points": [v(45.75, 28.13) * mm, v(45.12, 28.3) * mm, v(44.88, 28.96) * mm, v(45.24, 29.51) * mm]});
            skLineSegment(sketch, "E501", {"start": v(42.66, 26.3) * mm, "end": v(42.66, 25.1) * mm});
            skLineSegment(sketch, "E502", {"start": v(42.66, 25.1) * mm, "end": v(44.55, 25.1) * mm});
            skLineSegment(sketch, "E503", {"start": v(44.55, 25.1) * mm, "end": v(46.45, 25.1) * mm});
            skLineSegment(sketch, "E504", {"start": v(46.45, 25.1) * mm, "end": v(46.44, 26.4) * mm});
            skFitSpline(sketch, "E505", {"points": [v(48.25, 29.87) * mm, v(51.36, 29.87) * mm, v(51.4, 29.86) * mm, v(51.33, 28.94) * mm]});
            skFitSpline(sketch, "E506", {"points": [v(51.33, 28.94) * mm, v(51.28, 28.4) * mm, v(51.07, 28.2) * mm, v(50.34, 27.99) * mm]});
            skFitSpline(sketch, "E507", {"points": [v(50.34, 27.99) * mm, v(50.11, 27.92) * mm, v(50.1, 27.61) * mm, v(50.1, 24.12) * mm]});
            skFitSpline(sketch, "E508", {"points": [v(50.1, 24.12) * mm, v(50.1, 20.63) * mm, v(50.11, 20.32) * mm, v(50.34, 20.25) * mm]});
            skFitSpline(sketch, "E509", {"points": [v(50.34, 20.25) * mm, v(51.06, 20.04) * mm, v(51.28, 19.83) * mm, v(51.32, 19.33) * mm]});
            skFitSpline(sketch, "E510", {"points": [v(51.32, 19.33) * mm, v(51.4, 18.41) * mm, v(51.27, 18.37) * mm, v(48.2, 18.37) * mm]});
            skLineSegment(sketch, "E511", {"start": v(45.24, 29.51) * mm, "end": v(45.47, 29.87) * mm});
            skLineSegment(sketch, "E512", {"start": v(45.47, 29.87) * mm, "end": v(48.25, 29.87) * mm});
            skFitSpline(sketch, "E513", {"points": [v(45.24, 18.73) * mm, v(44.88, 19.28) * mm, v(45.12, 19.94) * mm, v(45.75, 20.11) * mm]});
            skFitSpline(sketch, "E514", {"points": [v(45.75, 20.11) * mm, v(46.02, 20.19) * mm, v(46.28, 20.31) * mm, v(46.34, 20.4) * mm]});
            skFitSpline(sketch, "E515", {"points": [v(46.34, 20.4) * mm, v(46.4, 20.48) * mm, v(46.44, 21.16) * mm, v(46.44, 21.91) * mm]});
            skLineSegment(sketch, "E516", {"start": v(48.2, 18.37) * mm, "end": v(45.47, 18.37) * mm});
            skLineSegment(sketch, "E517", {"start": v(45.47, 18.37) * mm, "end": v(45.24, 18.73) * mm});
            skFitSpline(sketch, "E518", {"points": [v(42.66, 22) * mm, v(42.66, 20.63) * mm, v(42.8, 20.2) * mm, v(43.23, 20.2) * mm]});
            skFitSpline(sketch, "E519", {"points": [v(43.23, 20.2) * mm, v(43.9, 20.2) * mm, v(44.33, 19.08) * mm, v(43.84, 18.6) * mm]});
            skFitSpline(sketch, "E520", {"points": [v(43.84, 18.6) * mm, v(43.65, 18.4) * mm, v(42.95, 18.37) * mm, v(38.3, 18.37) * mm]});
            skLineSegment(sketch, "E521", {"start": v(46.44, 21.91) * mm, "end": v(46.45, 23.28) * mm});
            skLineSegment(sketch, "E522", {"start": v(46.45, 23.28) * mm, "end": v(44.55, 23.28) * mm});
            skLineSegment(sketch, "E523", {"start": v(44.55, 23.28) * mm, "end": v(42.66, 23.28) * mm});
            skLineSegment(sketch, "E524", {"start": v(42.66, 23.28) * mm, "end": v(42.66, 22) * mm});
            skFitSpline(sketch, "E525", {"points": [v(32.77, 18.72) * mm, v(32.61, 18.95) * mm, v(32.57, 19.2) * mm, v(32.64, 19.49) * mm]});
            skFitSpline(sketch, "E526", {"points": [v(32.64, 19.49) * mm, v(32.74, 19.96) * mm, v(33.06, 20.2) * mm, v(33.6, 20.2) * mm]});
            skFitSpline(sketch, "E527", {"points": [v(33.6, 20.2) * mm, v(34.06, 20.2) * mm, v(34.06, 20.34) * mm, v(33.63, 21.47) * mm]});
            skLineSegment(sketch, "E528", {"start": v(38.3, 18.37) * mm, "end": v(33, 18.37) * mm});
            skLineSegment(sketch, "E529", {"start": v(33, 18.37) * mm, "end": v(32.77, 18.72) * mm});
            skFitSpline(sketch, "E530", {"points": [v(30.38, 21.53) * mm, v(29.95, 20.41) * mm, v(29.95, 20.2) * mm, v(30.4, 20.2) * mm]});
            skFitSpline(sketch, "E531", {"points": [v(30.4, 20.2) * mm, v(30.87, 20.2) * mm, v(31.3, 19.73) * mm, v(31.3, 19.22) * mm]});
            skFitSpline(sketch, "E532", {"points": [v(31.3, 19.22) * mm, v(31.3, 18.45) * mm, v(31.08, 18.37) * mm, v(28.76, 18.37) * mm]});
            skLineSegment(sketch, "E533", {"start": v(33.63, 21.47) * mm, "end": v(33.3, 22.37) * mm});
            skLineSegment(sketch, "E534", {"start": v(33.3, 22.37) * mm, "end": v(32, 22.37) * mm});
            skLineSegment(sketch, "E535", {"start": v(32, 22.37) * mm, "end": v(30.7, 22.37) * mm});
            skLineSegment(sketch, "E536", {"start": v(30.7, 22.37) * mm, "end": v(30.38, 21.53) * mm});
            skFitSpline(sketch, "E537", {"points": [v(26.43, 18.78) * mm, v(26.21, 19.16) * mm, v(26.18, 19.17) * mm, v(25.87, 18.97) * mm]});
            skFitSpline(sketch, "E538", {"points": [v(25.87, 18.97) * mm, v(25.17, 18.5) * mm, v(24.02, 18.38) * mm, v(20.56, 18.37) * mm]});
            skFitSpline(sketch, "E539", {"points": [v(20.56, 18.37) * mm, v(17.64, 18.37) * mm, v(17.15, 18.4) * mm, v(17, 18.6) * mm]});
            skLineSegment(sketch, "E540", {"start": v(28.76, 18.37) * mm, "end": v(26.67, 18.37) * mm});
            skLineSegment(sketch, "E541", {"start": v(26.67, 18.37) * mm, "end": v(26.43, 18.78) * mm});
            skFitSpline(sketch, "E542", {"points": [v(23.68, 21.11) * mm, v(24.24, 22.47) * mm, v(23.5, 23.84) * mm, v(22.2, 23.84) * mm]});
            skLineSegment(sketch, "E543", {"start": v(17, 18.6) * mm, "end": v(17, 18.6) * mm});
            skFitSpline(sketch, "E544", {"points": [v(21.77, 22.26) * mm, v(21.77, 21.21) * mm, v(21.83, 20.61) * mm, v(21.94, 20.5) * mm]});
            skFitSpline(sketch, "E545", {"points": [v(21.94, 20.5) * mm, v(22.15, 20.3) * mm, v(22.82, 20.29) * mm, v(23.2, 20.49) * mm]});
            skLineSegment(sketch, "E546", {"start": v(22.2, 23.84) * mm, "end": v(21.77, 23.84) * mm});
            skLineSegment(sketch, "E547", {"start": v(21.77, 23.84) * mm, "end": v(21.77, 22.26) * mm});
            skFitSpline(sketch, "E548", {"points": [v(32.33, 25.03) * mm, v(32.22, 25.38) * mm, v(32.08, 25.66) * mm, v(32.03, 25.66) * mm]});
            skFitSpline(sketch, "E549", {"points": [v(32.03, 25.66) * mm, v(31.98, 25.66) * mm, v(31.83, 25.38) * mm, v(31.7, 25.03) * mm]});
            skFitSpline(sketch, "E550", {"points": [v(22.69, 25.87) * mm, v(23.88, 26.36) * mm, v(23.47, 28.19) * mm, v(22.17, 28.19) * mm]});
            skLineSegment(sketch, "E551", {"start": v(31.7, 25.03) * mm, "end": v(31.48, 24.4) * mm});
            skLineSegment(sketch, "E552", {"start": v(31.48, 24.4) * mm, "end": v(32.01, 24.4) * mm});
            skLineSegment(sketch, "E553", {"start": v(32.01, 24.4) * mm, "end": v(32.55, 24.4) * mm});
            skLineSegment(sketch, "E554", {"start": v(32.55, 24.4) * mm, "end": v(32.33, 25.03) * mm});
            skFitSpline(sketch, "E555", {"points": [v(21.77, 26.92) * mm, v(21.77, 25.52) * mm, v(21.8, 25.5) * mm, v(22.69, 25.87) * mm]});
            skLineSegment(sketch, "E556", {"start": v(22.17, 28.19) * mm, "end": v(21.77, 28.19) * mm});
            skLineSegment(sketch, "E557", {"start": v(21.77, 28.19) * mm, "end": v(21.77, 26.92) * mm});
            skFitSpline(sketch, "E558", {"points": [v(-12.58, 15.13) * mm, v(-11.75, 15.27) * mm, v(-11.24, 15.7) * mm, v(-11.37, 16.17) * mm]});
            skFitSpline(sketch, "E559", {"points": [v(-11.37, 16.17) * mm, v(-11.49, 16.64) * mm, v(-11.02, 16.91) * mm, v(-9.73, 17.1) * mm]});
            skFitSpline(sketch, "E560", {"points": [v(-9.73, 17.1) * mm, v(-9.06, 17.18) * mm, v(-8.21, 17.35) * mm, v(-7.84, 17.46) * mm]});
            skFitSpline(sketch, "E561", {"points": [v(-7.84, 17.46) * mm, v(-6.87, 17.74) * mm, v(-5.1, 17.95) * mm, v(-3.73, 17.95) * mm]});
            skFitSpline(sketch, "E562", {"points": [v(-3.73, 17.95) * mm, v(-2.6, 17.95) * mm, v(-2.5, 17.98) * mm, v(-2.3, 18.29) * mm]});
            skFitSpline(sketch, "E563", {"points": [v(-2.3, 18.29) * mm, v(-1.92, 18.85) * mm, v(-1.88, 19.32) * mm, v(-2.12, 19.93) * mm]});
            skFitSpline(sketch, "E564", {"points": [v(-2.12, 19.93) * mm, v(-2.31, 20.4) * mm, v(-2.33, 20.64) * mm, v(-2.2, 21.3) * mm]});
            skFitSpline(sketch, "E565", {"points": [v(-2.2, 21.3) * mm, v(-1.97, 22.6) * mm, v(-1.4, 23.23) * mm, v(1.1, 24.89) * mm]});
            skFitSpline(sketch, "E566", {"points": [v(1.1, 24.89) * mm, v(1.59, 25.2) * mm, v(1.98, 25.63) * mm, v(2.32, 26.2) * mm]});
            skFitSpline(sketch, "E567", {"points": [v(2.32, 26.2) * mm, v(3.01, 27.37) * mm, v(3.16, 27.9) * mm, v(3.05, 28.81) * mm]});
            skFitSpline(sketch, "E568", {"points": [v(3.05, 28.81) * mm, v(2.93, 29.75) * mm, v(2.49, 30.21) * mm, v(1.22, 30.7) * mm]});
            skFitSpline(sketch, "E569", {"points": [v(1.22, 30.7) * mm, v(0.77, 30.87) * mm, v(0.18, 31.1) * mm, v(-0.09, 31.22) * mm]});
            skFitSpline(sketch, "E570", {"points": [v(-0.09, 31.22) * mm, v(-0.35, 31.33) * mm, v(-1.08, 31.49) * mm, v(-1.7, 31.56) * mm]});
            skFitSpline(sketch, "E571", {"points": [v(-1.7, 31.56) * mm, v(-4.13, 31.83) * mm, v(-5.2, 32.17) * mm, v(-6.6, 33.1) * mm]});
            skFitSpline(sketch, "E572", {"points": [v(-6.6, 33.1) * mm, v(-7.21, 33.51) * mm, v(-7.56, 33.65) * mm, v(-7.98, 33.65) * mm]});
            skFitSpline(sketch, "E573", {"points": [v(-7.98, 33.65) * mm, v(-8.3, 33.65) * mm, v(-9.18, 33.75) * mm, v(-9.96, 33.86) * mm]});
            skFitSpline(sketch, "E574", {"points": [v(-9.96, 33.86) * mm, v(-11.85, 34.13) * mm, v(-17.73, 34.5) * mm, v(-20.36, 34.52) * mm]});
            skFitSpline(sketch, "E575", {"points": [v(-20.36, 34.52) * mm, v(-21.51, 34.53) * mm, v(-23.19, 34.61) * mm, v(-24.07, 34.7) * mm]});
            skFitSpline(sketch, "E576", {"points": [v(-24.07, 34.7) * mm, v(-24.96, 34.8) * mm, v(-26.01, 34.84) * mm, v(-26.41, 34.79) * mm]});
            skFitSpline(sketch, "E577", {"points": [v(-26.41, 34.79) * mm, v(-26.8, 34.73) * mm, v(-27.5, 34.73) * mm, v(-27.95, 34.8) * mm]});
            skFitSpline(sketch, "E578", {"points": [v(-27.95, 34.8) * mm, v(-28.4, 34.85) * mm, v(-30.63, 34.96) * mm, v(-32.9, 35.05) * mm]});
            skFitSpline(sketch, "E579", {"points": [v(-32.9, 35.05) * mm, v(-35.18, 35.13) * mm, v(-37.7, 35.26) * mm, v(-38.51, 35.34) * mm]});
            skFitSpline(sketch, "E580", {"points": [v(-38.51, 35.34) * mm, v(-39.32, 35.41) * mm, v(-40.77, 35.5) * mm, v(-41.74, 35.55) * mm]});
            skFitSpline(sketch, "E581", {"points": [v(-41.74, 35.55) * mm, v(-43.61, 35.64) * mm, v(-44, 35.55) * mm, v(-44, 34.98) * mm]});
            skFitSpline(sketch, "E582", {"points": [v(-44, 34.98) * mm, v(-44, 34.25) * mm, v(-43.6, 30.2) * mm, v(-43.52, 30.05) * mm]});
            skFitSpline(sketch, "E583", {"points": [v(-43.52, 30.05) * mm, v(-43.4, 29.88) * mm, v(-42.99, 27.05) * mm, v(-42.93, 26.08) * mm]});
            skFitSpline(sketch, "E584", {"points": [v(-42.93, 26.08) * mm, v(-42.9, 25.65) * mm, v(-42.99, 25.23) * mm, v(-43.21, 24.75) * mm]});
            skFitSpline(sketch, "E585", {"points": [v(-43.21, 24.75) * mm, v(-43.4, 24.37) * mm, v(-43.65, 23.68) * mm, v(-43.78, 23.22) * mm]});
            skFitSpline(sketch, "E586", {"points": [v(-43.78, 23.22) * mm, v(-44, 22.43) * mm, v(-44.83, 20.5) * mm, v(-45.89, 18.29) * mm]});
            skFitSpline(sketch, "E587", {"points": [v(-45.89, 18.29) * mm, v(-46.15, 17.74) * mm, v(-46.36, 17.22) * mm, v(-46.36, 17.13) * mm]});
            skFitSpline(sketch, "E588", {"points": [v(-46.36, 17.13) * mm, v(-46.36, 17.04) * mm, v(-46.53, 16.64) * mm, v(-46.72, 16.25) * mm]});
            skFitSpline(sketch, "E589", {"points": [v(-46.72, 16.25) * mm, v(-46.92, 15.86) * mm, v(-47.06, 15.53) * mm, v(-47.04, 15.5) * mm]});
            skFitSpline(sketch, "E590", {"points": [v(-47.04, 15.5) * mm, v(-46.93, 15.42) * mm, v(-38.89, 15.14) * mm, v(-36.34, 15.13) * mm]});
            skFitSpline(sketch, "E591", {"points": [v(-36.34, 15.13) * mm, v(-34.8, 15.12) * mm, v(-32.97, 15.07) * mm, v(-32.27, 15.02) * mm]});
            skFitSpline(sketch, "E592", {"points": [v(-32.27, 15.02) * mm, v(-30.5, 14.88) * mm, v(-13.5, 14.97) * mm, v(-12.58, 15.13) * mm]});
            skFitSpline(sketch, "E593", {"points": [v(-12.06, 18.6) * mm, v(-12.12, 18.66) * mm, v(-14.07, 18.73) * mm, v(-16.39, 18.74) * mm]});
            skFitSpline(sketch, "E594", {"points": [v(-16.39, 18.74) * mm, v(-19.23, 18.76) * mm, v(-20.65, 18.82) * mm, v(-20.76, 18.93) * mm]});
            skFitSpline(sketch, "E595", {"points": [v(-20.76, 18.93) * mm, v(-20.84, 19.01) * mm, v(-20.91, 19.34) * mm, v(-20.91, 19.65) * mm]});
            skFitSpline(sketch, "E596", {"points": [v(-20.91, 19.65) * mm, v(-20.91, 20.3) * mm, v(-20.61, 20.62) * mm, v(-19.98, 20.62) * mm]});
            skFitSpline(sketch, "E597", {"points": [v(-19.98, 20.62) * mm, v(-19.48, 20.62) * mm, v(-19.47, 20.84) * mm, v(-19.92, 22.04) * mm]});
            skLineSegment(sketch, "E598", {"start": v(-12.58, 15.13) * mm, "end": v(-12.58, 15.13) * mm});
            skFitSpline(sketch, "E599", {"points": [v(-23.3, 22.02) * mm, v(-23.72, 20.94) * mm, v(-23.7, 20.62) * mm, v(-23.2, 20.62) * mm]});
            skFitSpline(sketch, "E600", {"points": [v(-23.2, 20.62) * mm, v(-22.63, 20.62) * mm, v(-22.35, 20.3) * mm, v(-22.35, 19.65) * mm]});
            skFitSpline(sketch, "E601", {"points": [v(-22.35, 19.65) * mm, v(-22.35, 19.32) * mm, v(-22.41, 19) * mm, v(-22.49, 18.92) * mm]});
            skFitSpline(sketch, "E602", {"points": [v(-22.49, 18.92) * mm, v(-22.56, 18.84) * mm, v(-24.47, 18.78) * mm, v(-27.08, 18.77) * mm]});
            skFitSpline(sketch, "E603", {"points": [v(-27.08, 18.77) * mm, v(-31.26, 18.75) * mm, v(-31.56, 18.77) * mm, v(-31.74, 19) * mm]});
            skFitSpline(sketch, "E604", {"points": [v(-31.74, 19) * mm, v(-31.91, 19.25) * mm, v(-31.93, 19.25) * mm, v(-32.1, 19.02) * mm]});
            skFitSpline(sketch, "E605", {"points": [v(-32.1, 19.02) * mm, v(-32.26, 18.8) * mm, v(-32.57, 18.78) * mm, v(-34.94, 18.77) * mm]});
            skFitSpline(sketch, "E606", {"points": [v(-34.94, 18.77) * mm, v(-36.4, 18.77) * mm, v(-37.74, 18.78) * mm, v(-37.92, 18.78) * mm]});
            skFitSpline(sketch, "E607", {"points": [v(-37.92, 18.78) * mm, v(-38.31, 18.8) * mm, v(-38.56, 19.37) * mm, v(-38.43, 19.95) * mm]});
            skFitSpline(sketch, "E608", {"points": [v(-38.43, 19.95) * mm, v(-38.37, 20.26) * mm, v(-38.2, 20.42) * mm, v(-37.73, 20.62) * mm]});
            skLineSegment(sketch, "E609", {"start": v(-19.92, 22.04) * mm, "end": v(-20.26, 22.93) * mm});
            skLineSegment(sketch, "E610", {"start": v(-20.26, 22.93) * mm, "end": v(-21.58, 22.97) * mm});
            skLineSegment(sketch, "E611", {"start": v(-21.58, 22.97) * mm, "end": v(-22.9, 23) * mm});
            skLineSegment(sketch, "E612", {"start": v(-22.9, 23) * mm, "end": v(-23.3, 22.02) * mm});
            skFitSpline(sketch, "E613", {"points": [v(-37.11, 24.66) * mm, v(-37.11, 28.7) * mm, v(-37.1, 28.62) * mm, v(-37.85, 28.8) * mm]});
            skFitSpline(sketch, "E614", {"points": [v(-37.85, 28.8) * mm, v(-38.52, 28.96) * mm, v(-38.71, 30.25) * mm, v(-38.12, 30.55) * mm]});
            skFitSpline(sketch, "E615", {"points": [v(-38.12, 30.55) * mm, v(-37.99, 30.6) * mm, v(-36.63, 30.65) * mm, v(-35.1, 30.64) * mm]});
            skFitSpline(sketch, "E616", {"points": [v(-35.1, 30.64) * mm, v(-32.55, 30.62) * mm, v(-32.29, 30.6) * mm, v(-32.11, 30.36) * mm]});
            skFitSpline(sketch, "E617", {"points": [v(-32.11, 30.36) * mm, v(-31.69, 29.77) * mm, v(-32.09, 28.75) * mm, v(-32.75, 28.75) * mm]});
            skFitSpline(sketch, "E618", {"points": [v(-32.75, 28.75) * mm, v(-33.24, 28.75) * mm, v(-33.34, 28.42) * mm, v(-33.3, 26.94) * mm]});
            skLineSegment(sketch, "E619", {"start": v(-37.73, 20.62) * mm, "end": v(-37.11, 20.89) * mm});
            skLineSegment(sketch, "E620", {"start": v(-37.11, 20.89) * mm, "end": v(-37.11, 24.66) * mm});
            skFitSpline(sketch, "E621", {"points": [v(-32.62, 26.03) * mm, v(-32.03, 26.5) * mm, v(-30.68, 28.23) * mm, v(-30.67, 28.54) * mm]});
            skFitSpline(sketch, "E622", {"points": [v(-30.67, 28.54) * mm, v(-30.66, 28.62) * mm, v(-30.85, 28.76) * mm, v(-31.08, 28.84) * mm]});
            skFitSpline(sketch, "E623", {"points": [v(-31.08, 28.84) * mm, v(-31.81, 29.12) * mm, v(-31.93, 30.2) * mm, v(-31.26, 30.54) * mm]});
            skFitSpline(sketch, "E624", {"points": [v(-31.26, 30.54) * mm, v(-31.13, 30.6) * mm, v(-30.01, 30.65) * mm, v(-28.79, 30.64) * mm]});
            skFitSpline(sketch, "E625", {"points": [v(-28.79, 30.64) * mm, v(-26.78, 30.63) * mm, v(-26.54, 30.6) * mm, v(-26.37, 30.36) * mm]});
            skFitSpline(sketch, "E626", {"points": [v(-26.37, 30.36) * mm, v(-25.9, 29.72) * mm, v(-26.35, 28.75) * mm, v(-27.12, 28.74) * mm]});
            skFitSpline(sketch, "E627", {"points": [v(-27.12, 28.74) * mm, v(-27.33, 28.74) * mm, v(-27.65, 28.66) * mm, v(-27.83, 28.56) * mm]});
            skFitSpline(sketch, "E628", {"points": [v(-27.83, 28.56) * mm, v(-28.3, 28.3) * mm, v(-30.16, 25.5) * mm, v(-30.01, 25.3) * mm]});
            skFitSpline(sketch, "E629", {"points": [v(-30.01, 25.3) * mm, v(-29.52, 24.63) * mm, v(-27.26, 21.85) * mm, v(-26.8, 21.34) * mm]});
            skLineSegment(sketch, "E630", {"start": v(-33.3, 26.94) * mm, "end": v(-33.26, 25.53) * mm});
            skLineSegment(sketch, "E631", {"start": v(-33.26, 25.53) * mm, "end": v(-32.62, 26.03) * mm});
            skFitSpline(sketch, "E632", {"points": [v(-25.96, 21.09) * mm, v(-25.83, 21.3) * mm, v(-25.03, 23.2) * mm, v(-24.2, 25.33) * mm]});
            skFitSpline(sketch, "E633", {"points": [v(-24.2, 25.33) * mm, v(-23.06, 28.22) * mm, v(-22.68, 29.34) * mm, v(-22.7, 29.76) * mm]});
            skFitSpline(sketch, "E634", {"points": [v(-22.7, 29.76) * mm, v(-22.73, 30.62) * mm, v(-22.48, 30.74) * mm, v(-20.75, 30.68) * mm]});
            skFitSpline(sketch, "E635", {"points": [v(-20.75, 30.68) * mm, v(-19.95, 30.66) * mm, v(-19.25, 30.57) * mm, v(-19.16, 30.48) * mm]});
            skFitSpline(sketch, "E636", {"points": [v(-19.16, 30.48) * mm, v(-19.08, 30.4) * mm, v(-18.32, 28.5) * mm, v(-17.47, 26.28) * mm]});
            skFitSpline(sketch, "E637", {"points": [v(-17.47, 26.28) * mm, v(-16.63, 24.05) * mm, v(-15.8, 21.92) * mm, v(-15.62, 21.53) * mm]});
            skLineSegment(sketch, "E638", {"start": v(-26.8, 21.34) * mm, "end": v(-26.21, 20.7) * mm});
            skLineSegment(sketch, "E639", {"start": v(-26.21, 20.7) * mm, "end": v(-25.96, 21.09) * mm});
            skFitSpline(sketch, "E640", {"points": [v(-15.24, 21.88) * mm, v(-15.17, 22.87) * mm, v(-15.15, 22.93) * mm, v(-14.78, 23.06) * mm]});
            skFitSpline(sketch, "E641", {"points": [v(-13.38, 22.23) * mm, v(-13.23, 21.84) * mm, v(-12.98, 21.38) * mm, v(-12.81, 21.2) * mm]});
            skFitSpline(sketch, "E642", {"points": [v(-12.81, 21.2) * mm, v(-11.94, 20.26) * mm, v(-10.53, 20.22) * mm, v(-10.19, 21.12) * mm]});
            skFitSpline(sketch, "E643", {"points": [v(-10.19, 21.12) * mm, v(-9.95, 21.74) * mm, v(-10.35, 22.21) * mm, v(-12.1, 23.36) * mm]});
            skFitSpline(sketch, "E644", {"points": [v(-12.1, 23.36) * mm, v(-14.02, 24.62) * mm, v(-14.7, 25.28) * mm, v(-14.95, 26.1) * mm]});
            skFitSpline(sketch, "E645", {"points": [v(-14.95, 26.1) * mm, v(-15.2, 26.93) * mm, v(-15.17, 28) * mm, v(-14.89, 28.72) * mm]});
            skFitSpline(sketch, "E646", {"points": [v(-14.89, 28.72) * mm, v(-14.24, 30.32) * mm, v(-12, 31.19) * mm, v(-9.9, 30.65) * mm]});
            skFitSpline(sketch, "E647", {"points": [v(-9.9, 30.65) * mm, v(-9.2, 30.47) * mm, v(-8.93, 30.45) * mm, v(-8.62, 30.58) * mm]});
            skFitSpline(sketch, "E648", {"points": [v(-8.62, 30.58) * mm, v(-8.15, 30.78) * mm, v(-7.58, 30.65) * mm, v(-7.4, 30.32) * mm]});
            skFitSpline(sketch, "E649", {"points": [v(-7.4, 30.32) * mm, v(-7.18, 29.9) * mm, v(-6.96, 27.25) * mm, v(-7.1, 26.85) * mm]});
            skFitSpline(sketch, "E650", {"points": [v(-7.1, 26.85) * mm, v(-7.24, 26.52) * mm, v(-7.3, 26.5) * mm, v(-7.91, 26.53) * mm]});
            skFitSpline(sketch, "E651", {"points": [v(-7.91, 26.53) * mm, v(-8.58, 26.57) * mm, v(-8.58, 26.58) * mm, v(-9, 27.41) * mm]});
            skFitSpline(sketch, "E652", {"points": [v(-9, 27.41) * mm, v(-9.48, 28.36) * mm, v(-10.13, 28.89) * mm, v(-10.83, 28.89) * mm]});
            skFitSpline(sketch, "E653", {"points": [v(-10.83, 28.89) * mm, v(-11.3, 28.89) * mm, v(-11.74, 28.6) * mm, v(-11.74, 28.28) * mm]});
            skFitSpline(sketch, "E654", {"points": [v(-11.74, 28.28) * mm, v(-11.74, 27.9) * mm, v(-11.24, 27.46) * mm, v(-9.89, 26.62) * mm]});
            skFitSpline(sketch, "E655", {"points": [v(-9.89, 26.62) * mm, v(-7.3, 25) * mm, v(-6.55, 24.06) * mm, v(-6.55, 22.38) * mm]});
            skFitSpline(sketch, "E656", {"points": [v(-6.55, 22.38) * mm, v(-6.55, 21.28) * mm, v(-6.77, 20.59) * mm, v(-7.36, 19.9) * mm]});
            skFitSpline(sketch, "E657", {"points": [v(-7.36, 19.9) * mm, v(-8.15, 18.99) * mm, v(-9.04, 18.61) * mm, v(-10.61, 18.54) * mm]});
            skFitSpline(sketch, "E658", {"points": [v(-10.61, 18.54) * mm, v(-11.35, 18.51) * mm, v(-12, 18.54) * mm, v(-12.06, 18.6) * mm]});
            skLineSegment(sketch, "E659", {"start": v(-15.62, 21.53) * mm, "end": v(-15.31, 20.84) * mm});
            skLineSegment(sketch, "E660", {"start": v(-15.31, 20.84) * mm, "end": v(-15.24, 21.88) * mm});
            skFitSpline(sketch, "E661", {"points": [v(-31.78, 20.2) * mm, v(-31.78, 20.27) * mm, v(-31.62, 20.41) * mm, v(-31.43, 20.51) * mm]});
            skLineSegment(sketch, "E662", {"start": v(-12.06, 18.6) * mm, "end": v(-12.06, 18.6) * mm});
            skFitSpline(sketch, "E663", {"points": [v(-31.76, 21.6) * mm, v(-32.14, 22.1) * mm, v(-32.65, 22.7) * mm, v(-32.89, 22.92) * mm]});
            skLineSegment(sketch, "E664", {"start": v(-31.43, 20.51) * mm, "end": v(-31.07, 20.7) * mm});
            skLineSegment(sketch, "E665", {"start": v(-31.07, 20.7) * mm, "end": v(-31.76, 21.6) * mm});
            skFitSpline(sketch, "E666", {"points": [v(-33.32, 22.22) * mm, v(-33.32, 21.6) * mm, v(-33.27, 21.03) * mm, v(-33.22, 20.95) * mm]});
            skFitSpline(sketch, "E667", {"points": [v(-33.22, 20.95) * mm, v(-33.16, 20.86) * mm, v(-32.88, 20.69) * mm, v(-32.59, 20.57) * mm]});
            skFitSpline(sketch, "E668", {"points": [v(-32.59, 20.57) * mm, v(-32.3, 20.45) * mm, v(-32.06, 20.28) * mm, v(-32.06, 20.2) * mm]});
            skFitSpline(sketch, "E669", {"points": [v(-32.06, 20.2) * mm, v(-32.06, 20.12) * mm, v(-32, 20.05) * mm, v(-31.92, 20.05) * mm]});
            skFitSpline(sketch, "E670", {"points": [v(-31.92, 20.05) * mm, v(-31.85, 20.05) * mm, v(-31.78, 20.12) * mm, v(-31.78, 20.2) * mm]});
            skLineSegment(sketch, "E671", {"start": v(-32.89, 22.92) * mm, "end": v(-33.33, 23.33) * mm});
            skLineSegment(sketch, "E672", {"start": v(-33.33, 23.33) * mm, "end": v(-33.32, 22.22) * mm});
            skFitSpline(sketch, "E673", {"points": [v(-21.18, 25.42) * mm, v(-21.29, 25.67) * mm, v(-21.41, 26) * mm, v(-21.47, 26.15) * mm]});
            skFitSpline(sketch, "E674", {"points": [v(-21.47, 26.15) * mm, v(-21.56, 26.4) * mm, v(-21.59, 26.4) * mm, v(-21.75, 26) * mm]});
            skFitSpline(sketch, "E675", {"points": [v(-21.75, 26) * mm, v(-22.19, 24.98) * mm, v(-22.18, 24.96) * mm, v(-21.57, 24.96) * mm]});
            skLineSegment(sketch, "E676", {"start": v(-31.78, 20.2) * mm, "end": v(-31.78, 20.2) * mm});
            skFitSpline(sketch, "E677", {"points": [v(31.97, -10) * mm, v(31.83, -9.87) * mm, v(31.84, -9.39) * mm, v(31.98, -9.39) * mm]});
            skFitSpline(sketch, "E678", {"points": [v(31.98, -9.39) * mm, v(32.1, -9.39) * mm, v(34.28, -6.96) * mm, v(35.83, -5.11) * mm]});
            skFitSpline(sketch, "E679", {"points": [v(35.83, -5.11) * mm, v(37.17, -3.5) * mm, v(37.41, -3.37) * mm, v(39.03, -3.3) * mm]});
            skLineSegment(sketch, "E680", {"start": v(-21.57, 24.96) * mm, "end": v(-21, 24.96) * mm});
            skLineSegment(sketch, "E681", {"start": v(-21, 24.96) * mm, "end": v(-21.18, 25.42) * mm});
            skFitSpline(sketch, "E682", {"points": [v(40.87, -3.72) * mm, v(41.54, -4.33) * mm, v(41.68, -4.61) * mm, v(41.68, -5.37) * mm]});
            skFitSpline(sketch, "E683", {"points": [v(41.68, -5.37) * mm, v(41.68, -5.9) * mm, v(41.6, -6.06) * mm, v(41.15, -6.5) * mm]});
            skFitSpline(sketch, "E684", {"points": [v(41.15, -6.5) * mm, v(40.83, -6.82) * mm, v(40.35, -7.1) * mm, v(39.9, -7.23) * mm]});
            skFitSpline(sketch, "E685", {"points": [v(39.9, -7.23) * mm, v(39.5, -7.34) * mm, v(39.1, -7.53) * mm, v(39.01, -7.64) * mm]});
            skFitSpline(sketch, "E686", {"points": [v(39.01, -7.64) * mm, v(38.92, -7.75) * mm, v(38.7, -7.84) * mm, v(38.51, -7.84) * mm]});
            skFitSpline(sketch, "E687", {"points": [v(38.51, -7.84) * mm, v(38.34, -7.84) * mm, v(38.02, -8) * mm, v(37.81, -8.2) * mm]});
            skFitSpline(sketch, "E688", {"points": [v(37.81, -8.2) * mm, v(37.6, -8.39) * mm, v(37.32, -8.55) * mm, v(37.2, -8.55) * mm]});
            skFitSpline(sketch, "E689", {"points": [v(37.2, -8.55) * mm, v(37.06, -8.55) * mm, v(36.79, -8.67) * mm, v(36.6, -8.83) * mm]});
            skFitSpline(sketch, "E690", {"points": [v(36.6, -8.83) * mm, v(36.4, -8.98) * mm, v(36.02, -9.15) * mm, v(35.77, -9.2) * mm]});
            skFitSpline(sketch, "E691", {"points": [v(35.77, -9.2) * mm, v(35.51, -9.25) * mm, v(35.12, -9.44) * mm, v(34.9, -9.62) * mm]});
            skFitSpline(sketch, "E692", {"points": [v(34.9, -9.62) * mm, v(34.58, -9.9) * mm, v(34.35, -9.95) * mm, v(33.57, -9.95) * mm]});
            skFitSpline(sketch, "E693", {"points": [v(33.57, -9.95) * mm, v(33.06, -9.95) * mm, v(32.5, -9.99) * mm, v(32.35, -10.03) * mm]});
            skFitSpline(sketch, "E694", {"points": [v(32.35, -10.03) * mm, v(32.2, -10.07) * mm, v(32.02, -10.06) * mm, v(31.97, -10) * mm]});
            skLineSegment(sketch, "E695", {"start": v(40.87, -3.72) * mm, "end": v(39.03, -3.3) * mm});
            skFitSpline(sketch, "E696", {"points": [v(36.7, -6.3) * mm, v(37.09, -6) * mm, v(37.53, -5.69) * mm, v(37.68, -5.62) * mm]});
            skFitSpline(sketch, "E697", {"points": [v(37.68, -5.62) * mm, v(38.14, -5.4) * mm, v(39.16, -4.47) * mm, v(39.16, -4.27) * mm]});
            skFitSpline(sketch, "E698", {"points": [v(39.16, -4.27) * mm, v(39.16, -3.96) * mm, v(38.96, -3.92) * mm, v(38.29, -4.1) * mm]});
            skFitSpline(sketch, "E699", {"points": [v(38.29, -4.1) * mm, v(37.77, -4.24) * mm, v(37.48, -4.47) * mm, v(36.66, -5.38) * mm]});
            skFitSpline(sketch, "E700", {"points": [v(36.66, -5.38) * mm, v(35.69, -6.45) * mm, v(35.45, -6.86) * mm, v(35.83, -6.86) * mm]});
            skFitSpline(sketch, "E701", {"points": [v(35.83, -6.86) * mm, v(35.92, -6.86) * mm, v(36.32, -6.61) * mm, v(36.7, -6.3) * mm]});
            skLineSegment(sketch, "E702", {"start": v(31.97, -10) * mm, "end": v(31.97, -10) * mm});
            skFitSpline(sketch, "E703", {"points": [v(-8.78, 36.5) * mm, v(-8.43, 35.48) * mm, v(-7.61, 33.93) * mm, v(-6.6, 33.1) * mm], "startDerivative": vector(0.99, -3.16) * mm, "endDerivative": vector(3.27, -2.09) * mm});
            skFitSpline(sketch, "E704", {"points": [v(5.78, 36.1) * mm, v(7.63, 35.26) * mm, v(10.11, 34.14) * mm, v(12.93, 33.51) * mm], "startDerivative": vector(5.97, -2.68) * mm, "endDerivative": vector(8.04, -1.36) * mm});
            skFitSpline(sketch, "E705", {"points": [v(-11.37, 16.17) * mm, v(-11.8, 14.6) * mm, v(-11.89, 13.01) * mm, v(-11.71, 11.88) * mm], "startDerivative": vector(-1.44, -4.37) * mm, "endDerivative": vector(0.75, -3.64) * mm});
            skFitSpline(sketch, "E706", {"points": [v(22.42, 15.43) * mm, v(22.78, 14.25) * mm, v(22.78, 12.37) * mm], "startDerivative": vector(1, -2.46) * mm, "endDerivative": vector(-0.22, -3.62) * mm});
            skFitSpline(sketch, "E707", {"points": [v(-18.71, 8.94) * mm, v(-19.16, 6.65) * mm, v(-19.07, 4.38) * mm, v(-18, 1.78) * mm], "startDerivative": vector(-1.64, -7.06) * mm, "endDerivative": vector(3.65, -7.36) * mm});
            skFitSpline(sketch, "E708", {"points": [v(-14.78, 23.06) * mm, v(-14.15, 23.06) * mm, v(-13.38, 22.23) * mm], "startDerivative": vector(1.51, 0.31) * mm, "endDerivative": vector(1.31, -1.87) * mm});
            skFitSpline(sketch, "E709", {"points": [v(23.68, 21.11) * mm, v(23.48, 20.76) * mm, v(23.2, 20.49) * mm], "startDerivative": vector(-0.35, -0.74) * mm, "endDerivative": vector(-0.61, -0.52) * mm});
            skFitSpline(sketch, "E710", {"points": [v(-2.3, 18.29) * mm, v(-2.3, 16.53) * mm], "startDerivative": vector(0, -1.75) * mm, "endDerivative": vector(0, -1.75) * mm});
            skFitSpline(sketch, "E711", {"points": [v(4.3, 18.4) * mm, v(4.63, 16.74) * mm], "startDerivative": vector(0.32, -1.66) * mm, "endDerivative": vector(0.32, -1.66) * mm});
            skPoint(sketch, "E712", {"position": v(23.4, -4.19) * mm});
            skPoint(sketch, "E713", {"position": v(21.6, -1.56) * mm});
            skPoint(sketch, "E714", {"position": v(19.87, 0.63) * mm});
            skLineSegment(sketch, "E715", {"start": v(-13.84, -1.89) * mm, "end": v(-23.84, -1.89) * mm});
            skLineSegment(sketch, "E716", {"start": v(-23.84, -1.89) * mm, "end": v(-23.86, -6.44) * mm});
            skLineSegment(sketch, "E717", {"start": v(-24.03, -25.39) * mm, "end": v(-23.93, -15.83) * mm});
            skLineSegment(sketch, "E718", {"start": v(17.9, -2.68) * mm, "end": v(20.14, -2.56) * mm});
            skLineSegment(sketch, "E719", {"start": v(31.7, -2.58) * mm, "end": v(39.03, -2.58) * mm});
            skPoint(sketch, "E720", {"position": v(39.01, -12.76) * mm});
            skLineSegment(sketch, "E721", {"start": v(39.01, -7.64) * mm, "end": v(39.01, -12.76) * mm});
            skLineSegment(sketch, "E722", {"start": v(38.95, -22.7) * mm, "end": v(38.95, -19.38) * mm});
            skLineSegment(sketch, "E723", {"start": v(9, -25.23) * mm, "end": v(11.25, -24.88) * mm});
            skLineSegment(sketch, "E724", {"start": v(17.57, -25.44) * mm, "end": v(22.89, -25.24) * mm});
            skLineSegment(sketch, "E725", {"start": v(39.03, -2.58) * mm, "end": v(39.03, -3.3) * mm});
            skPoint(sketch, "E726", {"position": v(-23.84, 12.36) * mm});
            skPoint(sketch, "E727", {"position": v(39.03, 11.84) * mm});
            skLineSegment(sketch, "E728", {"start": v(-23.84, -1.89) * mm, "end": v(-23.84, 12.36) * mm});
            skLineSegment(sketch, "E729", {"start": v(39.03, -2.58) * mm, "end": v(39.03, 11.84) * mm});
            skSolve(sketch);
        }
        {
            var Q0;
            {var subQ11=sQuery(id+"F0.wireOp",EDGE,"E354");Q0=makeQuery(id+"F0.imprint","IMPRINT",FACE,{"disambiguationData":[TD([[makeQuery(id+"F0.imprint","IMPRINT",EDGE,{"derivedFrom":subQ11}),-1.0]])]});}
            extrude(context, id + "F1", {"entities" : qUnion([Q0]), "depth" : 2.54 * mm, "offsetDistance" : 25.4 * mm});
        }
    });
